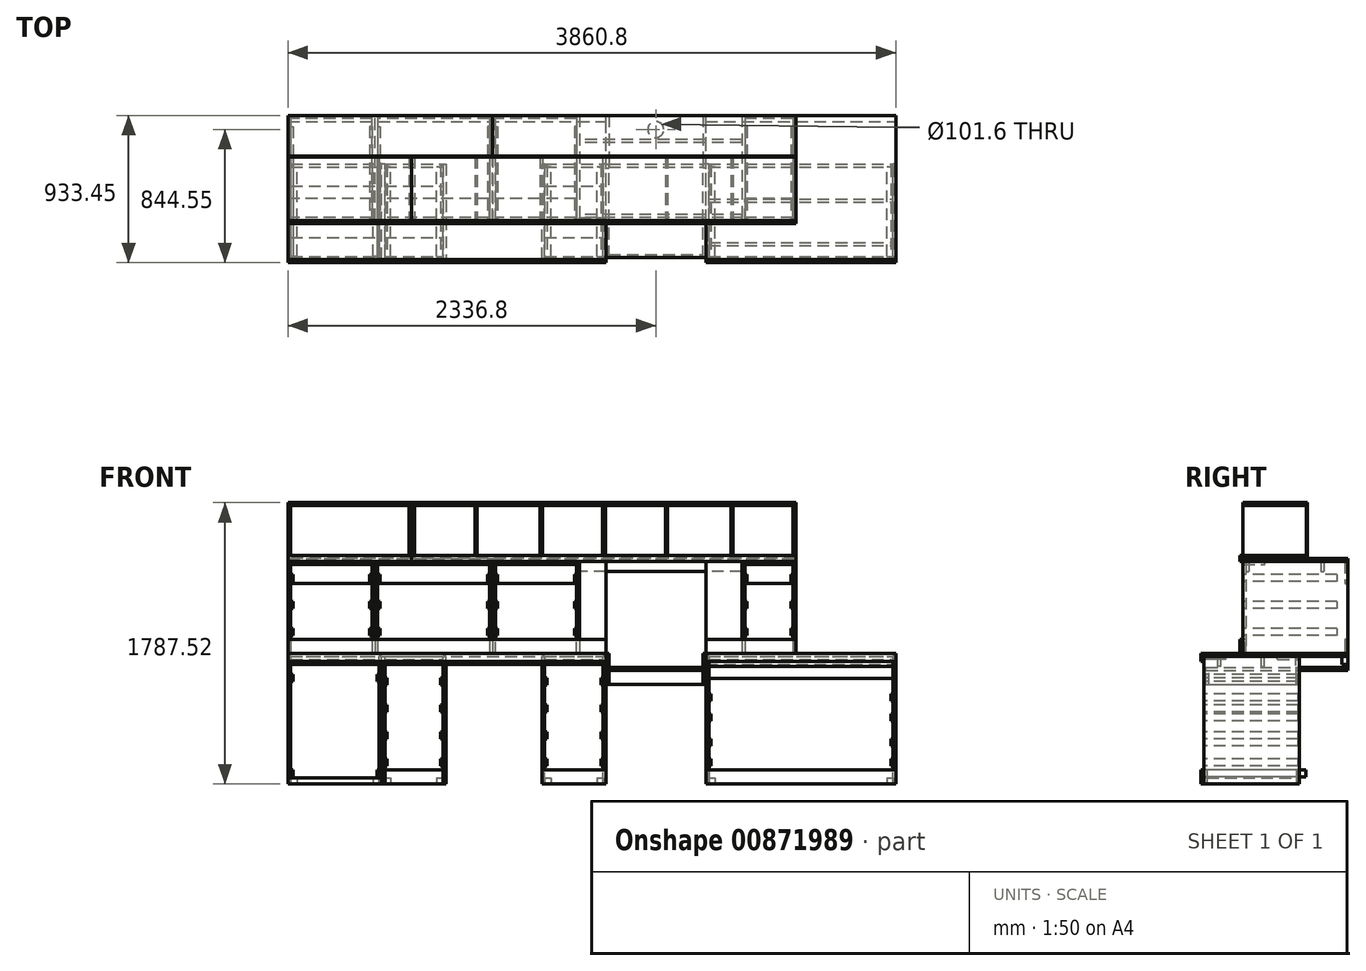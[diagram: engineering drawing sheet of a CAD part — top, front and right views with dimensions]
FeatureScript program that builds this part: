
annotation { "Feature Type Name" : "Feature", "Feature Type Description" : "" }
export const myFeature = defineFeature(function(context is Context, id is Id, definition is map)
    precondition{}
    {
        {
            var Q0;
            Q0=qCreatedBy(makeId("Top.planeOp"),FACE);
            var sketch = newSketch(context, id + "F0", { "sketchPlane" : qUnion([Q0])});
            skLineSegment(sketch, "E0.bottom", {"start": v(0, 0) * mm, "end": v(-19.05, 0) * mm});
            skLineSegment(sketch, "E0.top", {"start": v(0, 606.43) * mm, "end": v(-19.05, 606.43) * mm});
            skLineSegment(sketch, "E0.left", {"start": v(0, 0) * mm, "end": v(0, 606.43) * mm});
            skLineSegment(sketch, "E0.right", {"start": v(-19.05, 0) * mm, "end": v(-19.05, 606.43) * mm});
            skLineSegment(sketch, "E1.bottom", {"start": v(-1187.45, 0) * mm, "end": v(-1206.5, 0) * mm});
            skLineSegment(sketch, "E1.top", {"start": v(-1187.45, 606.42) * mm, "end": v(-1206.5, 606.42) * mm});
            skLineSegment(sketch, "E1.left", {"start": v(-1187.45, 0) * mm, "end": v(-1187.45, 606.42) * mm});
            skLineSegment(sketch, "E1.right", {"start": v(-1206.5, 0) * mm, "end": v(-1206.5, 606.42) * mm});
            skLineSegment(sketch, "E2.bottom", {"start": v(-1841.5, 0) * mm, "end": v(-1860.55, 0) * mm});
            skLineSegment(sketch, "E2.top", {"start": v(-1841.5, 606.42) * mm, "end": v(-1860.55, 606.42) * mm});
            skLineSegment(sketch, "E2.left", {"start": v(-1841.5, 0) * mm, "end": v(-1841.5, 606.42) * mm});
            skLineSegment(sketch, "E2.right", {"start": v(-1860.55, 0) * mm, "end": v(-1860.55, 606.42) * mm});
            skLineSegment(sketch, "E3.bottom", {"start": v(-2228.85, 0) * mm, "end": v(-2247.9, 0) * mm});
            skLineSegment(sketch, "E3.top", {"start": v(-2228.85, 606.42) * mm, "end": v(-2247.9, 606.42) * mm});
            skLineSegment(sketch, "E3.left", {"start": v(-2228.85, 0) * mm, "end": v(-2228.85, 606.42) * mm});
            skLineSegment(sketch, "E3.right", {"start": v(-2247.9, 0) * mm, "end": v(-2247.9, 606.42) * mm});
            skLineSegment(sketch, "E4.bottom", {"start": v(-2857.5, 0) * mm, "end": v(-2876.55, 0) * mm});
            skLineSegment(sketch, "E4.top", {"start": v(-2857.5, 606.42) * mm, "end": v(-2876.55, 606.42) * mm});
            skLineSegment(sketch, "E4.left", {"start": v(-2857.5, 0) * mm, "end": v(-2857.5, 606.42) * mm});
            skLineSegment(sketch, "E4.right", {"start": v(-2876.55, 0) * mm, "end": v(-2876.55, 606.42) * mm});
            skLineSegment(sketch, "E5.bottom", {"start": v(-3244.85, 0) * mm, "end": v(-3263.9, 0) * mm});
            skLineSegment(sketch, "E5.top", {"start": v(-3244.85, 606.42) * mm, "end": v(-3263.9, 606.42) * mm});
            skLineSegment(sketch, "E5.left", {"start": v(-3244.85, 0) * mm, "end": v(-3244.85, 606.42) * mm});
            skLineSegment(sketch, "E6", {"start": v(-3263.9, 606.42) * mm, "end": v(-3263.9, 0) * mm});
            skLineSegment(sketch, "E7.bottom", {"start": v(-3263.9, 0) * mm, "end": v(-3282.95, 0) * mm});
            skLineSegment(sketch, "E7.top", {"start": v(-3263.9, 606.42) * mm, "end": v(-3282.95, 606.42) * mm});
            skLineSegment(sketch, "E7.left", {"start": v(-3263.9, 0) * mm, "end": v(-3263.9, 606.42) * mm});
            skLineSegment(sketch, "E8", {"start": v(-3282.95, 606.42) * mm, "end": v(-3282.95, 0) * mm});
            skLineSegment(sketch, "E9.bottom", {"start": v(-3841.75, 0) * mm, "end": v(-3860.8, 0) * mm});
            skLineSegment(sketch, "E9.top", {"start": v(-3841.75, 606.42) * mm, "end": v(-3860.8, 606.42) * mm});
            skLineSegment(sketch, "E9.left", {"start": v(-3841.75, 0) * mm, "end": v(-3841.75, 606.42) * mm});
            skLineSegment(sketch, "E10", {"start": v(-3860.8, 606.42) * mm, "end": v(-3860.8, 0) * mm});
            skSolve(sketch);
        }
        {
            var Q0;
            Q0=makeQuery(id+"F0.imprint","IMPRINT",FACE,{"disambiguationData":[TD([[makeQuery(id+"F0.imprint","IMPRINT",EDGE,{"derivedFrom":sQuery(id+"F0.wireOp",EDGE,"E9.bottom")}),-1.0]])]});
            var Q1;
            Q1=makeQuery(id+"F0.imprint","IMPRINT",FACE,{"disambiguationData":[TD([[makeQuery(id+"F0.imprint","IMPRINT",EDGE,{"derivedFrom":sQuery(id+"F0.wireOp",EDGE,"E7.bottom")}),-1.0]])]});
            var Q2;
            Q2=makeQuery(id+"F0.imprint","IMPRINT",FACE,{"disambiguationData":[TD([[makeQuery(id+"F0.imprint","IMPRINT",EDGE,{"derivedFrom":sQuery(id+"F0.wireOp",EDGE,"E1.bottom")}),-1.0]])]});
            var Q3;
            Q3=makeQuery(id+"F0.imprint","IMPRINT",FACE,{"disambiguationData":[TD([[makeQuery(id+"F0.imprint","IMPRINT",EDGE,{"derivedFrom":sQuery(id+"F0.wireOp",EDGE,"E2.bottom")}),-1.0]])]});
            var Q4;
            Q4=makeQuery(id+"F0.imprint","IMPRINT",FACE,{"disambiguationData":[TD([[makeQuery(id+"F0.imprint","IMPRINT",EDGE,{"derivedFrom":sQuery(id+"F0.wireOp",EDGE,"E3.bottom")}),-1.0]])]});
            var Q5;
            Q5=makeQuery(id+"F0.imprint","IMPRINT",FACE,{"disambiguationData":[TD([[makeQuery(id+"F0.imprint","IMPRINT",EDGE,{"derivedFrom":sQuery(id+"F0.wireOp",EDGE,"E0.bottom")}),-1.0]])]});
            extrude(context, id + "F1", {"entities" : qUnion([Q0, Q1, Q2, Q3, Q4, Q5]), "oppositeDirection" : true, "depth" : 809.62 * mm, "offsetDistance" : 25.4 * mm});
        }
        {
            var Q0;
            Q0=qCreatedBy(makeId("Top.planeOp"),FACE);
            var sketch = newSketch(context, id + "F2", { "sketchPlane" : qUnion([Q0])});
            skPoint(sketch, "E11.0", {"position": v(-2857.5, 0) * mm});
            skPoint(sketch, "E11.1", {"position": v(-2876.55, 606.42) * mm});
            skLineSegment(sketch, "E12.bottom", {"start": v(-2857.5, 0) * mm, "end": v(-2876.55, 0) * mm});
            skLineSegment(sketch, "E12.top", {"start": v(-2857.5, 606.42) * mm, "end": v(-2876.55, 606.42) * mm});
            skLineSegment(sketch, "E12.left", {"start": v(-2857.5, 0) * mm, "end": v(-2857.5, 606.42) * mm});
            skLineSegment(sketch, "E12.right", {"start": v(-2876.55, 0) * mm, "end": v(-2876.55, 606.42) * mm});
            skPoint(sketch, "E13.0", {"position": v(-3263.9, 606.42) * mm});
            skPoint(sketch, "E13.1", {"position": v(-3244.85, 0) * mm});
            skLineSegment(sketch, "E14.bottom", {"start": v(-3263.9, 606.42) * mm, "end": v(-3244.85, 606.42) * mm});
            skLineSegment(sketch, "E14.top", {"start": v(-3263.9, 0) * mm, "end": v(-3244.85, 0) * mm});
            skLineSegment(sketch, "E14.left", {"start": v(-3263.9, 606.42) * mm, "end": v(-3263.9, 0) * mm});
            skLineSegment(sketch, "E14.right", {"start": v(-3244.85, 606.42) * mm, "end": v(-3244.85, 0) * mm});
            skSolve(sketch);
        }
        {
            var Q0;
            Q0 = qSketchRegion(id + "F2", true);
            var Q1;
            Q1=makeQuery(id+"F1.opExtrude","CAP_FACE",FACE,{"disambiguationData":[OSD([sQuery(id+"F0.wireOp",EDGE,"E7.bottom"),sQuery(id+"F0.wireOp",EDGE,"E7.top"),sQuery(id+"F0.wireOp",EDGE,"E7.left"),sQuery(id+"F0.wireOp",EDGE,"E8")])],"isStart":false});
            extrude(context, id + "F3", {"entities" : qUnion([Q0]), "endBound" : BoundingType.UP_TO_SURFACE, "oppositeDirection" : true, "depth" : 25.4 * mm, "endBoundEntityFace" : qUnion([Q1]), "offsetDistance" : 25.4 * mm});
        }
        {
            var Q0;
            Q0=makeQuery(id+"F1.opExtrude","SWEPT_FACE",FACE,{"disambiguationData":[OSD([sQuery(id+"F0.wireOp",EDGE,"E0.right")])]});
            var sketch = newSketch(context, id + "F4", { "sketchPlane" : qUnion([Q0])});
            skLineSegment(sketch, "E15.0", {"start": v(-606.43, -809.62) * mm, "end": v(-606.43, 0) * mm, "construction": true});
            skLineSegment(sketch, "E15.1", {"start": v(0, 0) * mm, "end": v(-606.43, 0) * mm, "construction": true});
            skLineSegment(sketch, "E15.2", {"start": v(0, -809.62) * mm, "end": v(0, 0) * mm, "construction": true});
            skLineSegment(sketch, "E16.bottom", {"start": v(-606.43, 0) * mm, "end": v(-587.38, 0) * mm});
            skLineSegment(sketch, "E16.top", {"start": v(-606.43, -139.7) * mm, "end": v(-587.38, -139.7) * mm});
            skLineSegment(sketch, "E16.left", {"start": v(-606.43, 0) * mm, "end": v(-606.43, -139.7) * mm});
            skLineSegment(sketch, "E16.right", {"start": v(-587.38, 0) * mm, "end": v(-587.38, -139.7) * mm});
            skLineSegment(sketch, "E17.bottom", {"start": v(-606.43, -809.62) * mm, "end": v(-587.38, -809.62) * mm});
            skLineSegment(sketch, "E17.top", {"start": v(-606.43, -720.73) * mm, "end": v(-587.38, -720.73) * mm});
            skLineSegment(sketch, "E17.left", {"start": v(-606.43, -809.62) * mm, "end": v(-606.43, -720.73) * mm});
            skLineSegment(sketch, "E17.right", {"start": v(-587.38, -809.62) * mm, "end": v(-587.38, -720.73) * mm});
            skLineSegment(sketch, "E18.bottom", {"start": v(0, 0) * mm, "end": v(-88.9, 0) * mm});
            skLineSegment(sketch, "E18.top", {"start": v(0, -19.05) * mm, "end": v(-88.9, -19.05) * mm});
            skLineSegment(sketch, "E18.left", {"start": v(0, 0) * mm, "end": v(0, -19.05) * mm});
            skLineSegment(sketch, "E18.right", {"start": v(-88.9, 0) * mm, "end": v(-88.9, -19.05) * mm});
            skLineSegment(sketch, "E19.bottom", {"start": v(0, -809.62) * mm, "end": v(-19.05, -809.62) * mm});
            skLineSegment(sketch, "E19.top", {"start": v(0, -720.73) * mm, "end": v(-19.05, -720.73) * mm});
            skLineSegment(sketch, "E19.left", {"start": v(0, -809.62) * mm, "end": v(0, -720.73) * mm});
            skLineSegment(sketch, "E19.right", {"start": v(-19.05, -809.62) * mm, "end": v(-19.05, -720.73) * mm});
            skSolve(sketch);
        }
        {
            var Q0;
            Q0 = qSketchRegion(id + "F4", true);
            var Q1;
            Q1=makeQuery(id+"F1.opExtrude","SWEPT_FACE",FACE,{"disambiguationData":[OSD([sQuery(id+"F0.wireOp",EDGE,"E1.left")])]});
            extrude(context, id + "F5", {"entities" : qUnion([Q0]), "endBound" : BoundingType.UP_TO_SURFACE, "depth" : 25.4 * mm, "endBoundEntityFace" : qUnion([Q1]), "offsetDistance" : 25.4 * mm});
        }
        {
            var Q0;
            Q0=makeQuery(id+"F1.opExtrude","SWEPT_FACE",FACE,{"disambiguationData":[OSD([sQuery(id+"F0.wireOp",EDGE,"E2.right")])]});
            var sketch = newSketch(context, id + "F6", { "sketchPlane" : qUnion([Q0])});
            skLineSegment(sketch, "E20.1", {"start": v(0, 0) * mm, "end": v(-606.42, 0) * mm, "construction": true});
            skLineSegment(sketch, "E21.bottom", {"start": v(-606.42, 0) * mm, "end": v(-466.72, 0) * mm});
            skLineSegment(sketch, "E21.top", {"start": v(-606.42, -19.05) * mm, "end": v(-466.72, -19.05) * mm});
            skLineSegment(sketch, "E21.left", {"start": v(-606.42, 0) * mm, "end": v(-606.42, -19.05) * mm});
            skLineSegment(sketch, "E21.right", {"start": v(-466.72, 0) * mm, "end": v(-466.72, -19.05) * mm});
            skLineSegment(sketch, "E22.bottom", {"start": v(-606.42, -809.62) * mm, "end": v(-587.37, -809.62) * mm});
            skLineSegment(sketch, "E22.top", {"start": v(-606.42, -720.73) * mm, "end": v(-587.37, -720.73) * mm});
            skLineSegment(sketch, "E22.left", {"start": v(-606.42, -809.62) * mm, "end": v(-606.42, -720.73) * mm});
            skLineSegment(sketch, "E22.right", {"start": v(-587.37, -809.62) * mm, "end": v(-587.37, -720.73) * mm});
            skLineSegment(sketch, "E23.bottom", {"start": v(0, 0) * mm, "end": v(-139.7, 0) * mm});
            skLineSegment(sketch, "E23.top", {"start": v(0, -19.05) * mm, "end": v(-139.7, -19.05) * mm});
            skLineSegment(sketch, "E23.left", {"start": v(0, 0) * mm, "end": v(0, -19.05) * mm});
            skLineSegment(sketch, "E23.right", {"start": v(-139.7, 0) * mm, "end": v(-139.7, -19.05) * mm});
            skLineSegment(sketch, "E24.bottom", {"start": v(0, -809.62) * mm, "end": v(-19.05, -809.62) * mm});
            skLineSegment(sketch, "E24.top", {"start": v(0, -720.73) * mm, "end": v(-19.05, -720.73) * mm});
            skLineSegment(sketch, "E24.left", {"start": v(0, -809.62) * mm, "end": v(0, -720.73) * mm});
            skLineSegment(sketch, "E24.right", {"start": v(-19.05, -809.62) * mm, "end": v(-19.05, -720.73) * mm});
            skSolve(sketch);
        }
        {
            var Q0;
            Q0 = qSketchRegion(id + "F6", true);
            var Q1;
            Q1=makeQuery(id+"F1.opExtrude","SWEPT_FACE",FACE,{"disambiguationData":[OSD([sQuery(id+"F0.wireOp",EDGE,"E3.left")])]});
            extrude(context, id + "F7", {"entities" : qUnion([Q0]), "endBound" : BoundingType.UP_TO_SURFACE, "depth" : 25.4 * mm, "endBoundEntityFace" : qUnion([Q1]), "offsetDistance" : 25.4 * mm});
        }
        {
            var Q0;
            Q0=makeQuery(id+"F1.opExtrude","SWEPT_FACE",FACE,{"disambiguationData":[OSD([sQuery(id+"F0.wireOp",EDGE,"E8")])]});
            var sketch = newSketch(context, id + "F8", { "sketchPlane" : qUnion([Q0])});
            skLineSegment(sketch, "E25.1", {"start": v(-606.42, 0) * mm, "end": v(0, 0) * mm, "construction": true});
            skLineSegment(sketch, "E26.bottom", {"start": v(-606.42, 0) * mm, "end": v(-466.72, 0) * mm});
            skLineSegment(sketch, "E26.top", {"start": v(-606.42, -19.05) * mm, "end": v(-466.72, -19.05) * mm});
            skLineSegment(sketch, "E26.left", {"start": v(-606.42, 0) * mm, "end": v(-606.42, -19.05) * mm});
            skLineSegment(sketch, "E26.right", {"start": v(-466.72, 0) * mm, "end": v(-466.72, -19.05) * mm});
            skLineSegment(sketch, "E27.bottom", {"start": v(-606.42, -809.62) * mm, "end": v(-587.37, -809.62) * mm});
            skLineSegment(sketch, "E27.top", {"start": v(-606.42, -771.53) * mm, "end": v(-587.37, -771.53) * mm});
            skLineSegment(sketch, "E27.left", {"start": v(-606.42, -809.62) * mm, "end": v(-606.42, -771.53) * mm});
            skLineSegment(sketch, "E27.right", {"start": v(-587.37, -809.62) * mm, "end": v(-587.37, -771.53) * mm});
            skLineSegment(sketch, "E28.bottom", {"start": v(0, 0) * mm, "end": v(-139.7, 0) * mm});
            skLineSegment(sketch, "E28.top", {"start": v(0, -19.05) * mm, "end": v(-139.7, -19.05) * mm});
            skLineSegment(sketch, "E28.left", {"start": v(0, 0) * mm, "end": v(0, -19.05) * mm});
            skLineSegment(sketch, "E28.right", {"start": v(-139.7, 0) * mm, "end": v(-139.7, -19.05) * mm});
            skLineSegment(sketch, "E29.bottom", {"start": v(0, -809.62) * mm, "end": v(-19.05, -809.62) * mm});
            skLineSegment(sketch, "E29.top", {"start": v(0, -771.53) * mm, "end": v(-19.05, -771.53) * mm});
            skLineSegment(sketch, "E29.left", {"start": v(0, -809.62) * mm, "end": v(0, -771.53) * mm});
            skLineSegment(sketch, "E29.right", {"start": v(-19.05, -809.62) * mm, "end": v(-19.05, -771.53) * mm});
            skSolve(sketch);
        }
        {
            var Q0;
            Q0 = qSketchRegion(id + "F8", true);
            var Q1;
            Q1=makeQuery(id+"F1.opExtrude","SWEPT_FACE",FACE,{"disambiguationData":[OSD([sQuery(id+"F0.wireOp",EDGE,"E9.left")])]});
            extrude(context, id + "F9", {"entities" : qUnion([Q0]), "endBound" : BoundingType.UP_TO_SURFACE, "depth" : 25.4 * mm, "endBoundEntityFace" : qUnion([Q1]), "offsetDistance" : 25.4 * mm});
        }
        {
            var Q0;
            Q0=makeQuery(id+"F1.opExtrude","SWEPT_FACE",FACE,{"disambiguationData":[OSD([sQuery(id+"F0.wireOp",EDGE,"E0.right")])]});
            var sketch = newSketch(context, id + "F10", { "sketchPlane" : qUnion([Q0])});
            skLineSegment(sketch, "E30.bottom", {"start": v(-384.18, 0) * mm, "end": v(-365.13, 0) * mm});
            skLineSegment(sketch, "E30.top", {"start": v(-384.18, -63.5) * mm, "end": v(-365.13, -63.5) * mm});
            skLineSegment(sketch, "E30.left", {"start": v(-384.18, 0) * mm, "end": v(-384.18, -63.5) * mm});
            skLineSegment(sketch, "E30.right", {"start": v(-365.13, 0) * mm, "end": v(-365.13, -63.5) * mm});
            skPoint(sketch, "E31.0", {"position": v(-88.9, 0) * mm});
            skLineSegment(sketch, "E32.bottom", {"start": v(-88.9, 0) * mm, "end": v(-107.95, 0) * mm});
            skLineSegment(sketch, "E32.top", {"start": v(-88.9, -63.5) * mm, "end": v(-107.95, -63.5) * mm});
            skLineSegment(sketch, "E32.left", {"start": v(-88.9, 0) * mm, "end": v(-88.9, -63.5) * mm});
            skLineSegment(sketch, "E32.right", {"start": v(-107.95, 0) * mm, "end": v(-107.95, -63.5) * mm});
            skSolve(sketch);
        }
        {
            var Q0;
            Q0 = qSketchRegion(id + "F10", true);
            var Q1;
            Q1=makeQuery(id+"F1.opExtrude","SWEPT_FACE",FACE,{"disambiguationData":[OSD([sQuery(id+"F0.wireOp",EDGE,"E1.left")])]});
            extrude(context, id + "F11", {"entities" : qUnion([Q0]), "endBound" : BoundingType.UP_TO_SURFACE, "depth" : 25.4 * mm, "endBoundEntityFace" : qUnion([Q1]), "offsetDistance" : 25.4 * mm});
        }
        {
            var Q0;
            Q0=qCreatedBy(makeId("Top.planeOp"),FACE);
            var sketch = newSketch(context, id + "F12", { "sketchPlane" : qUnion([Q0])});
            skPoint(sketch, "E33.0", {"position": v(-1206.5, 606.42) * mm});
            skLineSegment(sketch, "E34.bottom", {"start": v(0, 0) * mm, "end": v(-1206.5, 0) * mm});
            skLineSegment(sketch, "E34.top", {"start": v(0, 914.4) * mm, "end": v(-1206.5, 914.4) * mm});
            skLineSegment(sketch, "E34.left", {"start": v(0, 0) * mm, "end": v(0, 914.4) * mm});
            skLineSegment(sketch, "E34.right", {"start": v(-1206.5, 0) * mm, "end": v(-1206.5, 914.4) * mm});
            skPoint(sketch, "E35.0", {"position": v(-1841.5, 0) * mm});
            skPoint(sketch, "E35.1", {"position": v(-3860.8, 606.42) * mm});
            skLineSegment(sketch, "E36.bottom", {"start": v(-1841.5, 0) * mm, "end": v(-3860.8, 0) * mm});
            skLineSegment(sketch, "E36.top", {"start": v(-1841.5, 914.4) * mm, "end": v(-3860.8, 914.4) * mm});
            skLineSegment(sketch, "E36.left", {"start": v(-1841.5, 0) * mm, "end": v(-1841.5, 914.4) * mm});
            skLineSegment(sketch, "E36.right", {"start": v(-3860.8, 0) * mm, "end": v(-3860.8, 914.4) * mm});
            skLineSegment(sketch, "E37.0", {"start": v(-3860.8, 606.42) * mm, "end": v(-3860.8, 0) * mm, "construction": true});
            skLineSegment(sketch, "E38.0", {"start": v(-1206.5, 0) * mm, "end": v(-1206.5, 606.42) * mm, "construction": true});
            skSolve(sketch);
        }
        {
            var Q0;
            Q0 = qSketchRegion(id + "F12", true);
            extrude(context, id + "F13", {"entities" : qUnion([Q0]), "depth" : 19.05 * mm, "offsetDistance" : 25.4 * mm});
        }
        {
            var Q0;
            Q0=makeQuery(id+"F13.opExtrude","SWEPT_FACE",FACE,{"disambiguationData":[OSD([sQuery(id+"F12.wireOp",EDGE,"E34.left")])]});
            var sketch = newSketch(context, id + "F14", { "sketchPlane" : qUnion([Q0])});
            skLineSegment(sketch, "E39.bottom", {"start": v(876.3, 0) * mm, "end": v(914.4, 0) * mm});
            skLineSegment(sketch, "E39.top", {"start": v(876.3, -50.8) * mm, "end": v(914.4, -50.8) * mm});
            skLineSegment(sketch, "E39.left", {"start": v(876.3, 0) * mm, "end": v(876.3, -50.8) * mm});
            skLineSegment(sketch, "E39.right", {"start": v(914.4, 0) * mm, "end": v(914.4, -50.8) * mm});
            skSolve(sketch);
        }
        {
            var Q0;
            Q0 = qSketchRegion(id + "F14", true);
            var Q1;
            Q1=makeQuery(id+"F13.opExtrude","SWEPT_FACE",FACE,{"disambiguationData":[OSD([sQuery(id+"F12.wireOp",EDGE,"E34.right")])]});
            extrude(context, id + "F15", {"entities" : qUnion([Q0]), "endBound" : BoundingType.UP_TO_SURFACE, "oppositeDirection" : true, "depth" : 25.4 * mm, "endBoundEntityFace" : qUnion([Q1]), "offsetDistance" : 25.4 * mm});
        }
        {
            var Q0;
            Q0=makeQuery(id+"F13.opExtrude","SWEPT_FACE",FACE,{"disambiguationData":[OSD([sQuery(id+"F12.wireOp",EDGE,"E36.left")])]});
            var sketch = newSketch(context, id + "F16", { "sketchPlane" : qUnion([Q0])});
            skLineSegment(sketch, "E40.bottom", {"start": v(876.3, 0) * mm, "end": v(914.4, 0) * mm});
            skLineSegment(sketch, "E40.top", {"start": v(876.3, -50.8) * mm, "end": v(914.4, -50.8) * mm});
            skLineSegment(sketch, "E40.left", {"start": v(876.3, 0) * mm, "end": v(876.3, -50.8) * mm});
            skLineSegment(sketch, "E40.right", {"start": v(914.4, 0) * mm, "end": v(914.4, -50.8) * mm});
            skSolve(sketch);
        }
        {
            var Q0;
            Q0=makeQuery(id+"F16.imprint","IMPRINT",FACE,{"disambiguationData":[TD([[makeQuery(id+"F16.imprint","IMPRINT",EDGE,{"derivedFrom":sQuery(id+"F16.wireOp",EDGE,"E40.bottom")}),-1.0]])]});
            var Q1;
            Q1=makeQuery(id+"F13.opExtrude","SWEPT_FACE",FACE,{"disambiguationData":[OSD([sQuery(id+"F12.wireOp",EDGE,"E36.right")])]});
            extrude(context, id + "F17", {"entities" : qUnion([Q0]), "endBound" : BoundingType.UP_TO_SURFACE, "oppositeDirection" : true, "depth" : 25.4 * mm, "endBoundEntityFace" : qUnion([Q1]), "offsetDistance" : 25.4 * mm});
        }
        {
            var Q0;
            Q0=makeQuery(id+"F13.opExtrude","CAP_FACE",FACE,{"disambiguationData":[OSD([sQuery(id+"F12.wireOp",EDGE,"E34.bottom"),sQuery(id+"F12.wireOp",EDGE,"E34.top"),sQuery(id+"F12.wireOp",EDGE,"E34.left"),sQuery(id+"F12.wireOp",EDGE,"E34.right")])],"isStart":false});
            cPlane(context, id + "F18", {"entities" : qUnion([Q0]), "cplaneType" : CPlaneType.OFFSET, "offset" : 88.9 * mm, "oppositeDirection" : true, "width" : 152.4 * mm, "height" : 152.4 * mm});
        }
        {
            var Q0;
            Q0=qCreatedBy(id+"F18.planeOp",FACE);
            var sketch = newSketch(context, id + "F19", { "sketchPlane" : qUnion([Q0])});
            skLineSegment(sketch, "E41.0", {"start": v(-1841.5, 0) * mm, "end": v(-3860.8, 0) * mm, "construction": true});
            skLineSegment(sketch, "E41.1", {"start": v(0, 0) * mm, "end": v(-1206.5, 0) * mm, "construction": true});
            skLineSegment(sketch, "E41.2", {"start": v(-1206.5, 0) * mm, "end": v(-1206.5, 914.4) * mm, "construction": true});
            skLineSegment(sketch, "E41.3", {"start": v(-1841.5, 0) * mm, "end": v(-1841.5, 914.4) * mm, "construction": true});
            skLineSegment(sketch, "E42.bottom", {"start": v(-1841.5, 12.7) * mm, "end": v(-1206.5, 12.7) * mm});
            skLineSegment(sketch, "E42.top", {"start": v(-1841.5, 914.4) * mm, "end": v(-1206.5, 914.4) * mm});
            skLineSegment(sketch, "E42.left", {"start": v(-1841.5, 12.7) * mm, "end": v(-1841.5, 914.4) * mm});
            skLineSegment(sketch, "E42.right", {"start": v(-1206.5, 12.7) * mm, "end": v(-1206.5, 914.4) * mm});
            skSolve(sketch);
        }
        {
            var Q0;
            Q0=makeQuery(id+"F19.imprint","IMPRINT",FACE,{"disambiguationData":[TD([[makeQuery(id+"F19.imprint","IMPRINT",EDGE,{"derivedFrom":sQuery(id+"F19.wireOp",EDGE,"E42.bottom")}),1.0]])]});
            extrude(context, id + "F20", {"entities" : qUnion([Q0]), "oppositeDirection" : true, "depth" : 19.05 * mm, "offsetDistance" : 25.4 * mm});
        }
        {
            var Q0;
            Q0=makeQuery(id+"F20.opExtrude","CAP_FACE",FACE,{"disambiguationData":[OSD([sQuery(id+"F19.wireOp",EDGE,"E42.bottom"),sQuery(id+"F19.wireOp",EDGE,"E42.top"),sQuery(id+"F19.wireOp",EDGE,"E42.left"),sQuery(id+"F19.wireOp",EDGE,"E42.right")])],"isStart":false});
            var sketch = newSketch(context, id + "F21", { "sketchPlane" : qUnion([Q0])});
            skPoint(sketch, "E43.0", {"position": v(-1841.5, -606.42) * mm});
            skPoint(sketch, "E44.0", {"position": v(-1206.5, -606.42) * mm});
            skLineSegment(sketch, "E45.bottom", {"start": v(-1841.5, -12.7) * mm, "end": v(-1822.45, -12.7) * mm});
            skLineSegment(sketch, "E45.top", {"start": v(-1841.5, -606.42) * mm, "end": v(-1822.45, -606.42) * mm});
            skLineSegment(sketch, "E45.left", {"start": v(-1841.5, -12.7) * mm, "end": v(-1841.5, -606.42) * mm});
            skLineSegment(sketch, "E45.right", {"start": v(-1822.45, -12.7) * mm, "end": v(-1822.45, -606.42) * mm});
            skLineSegment(sketch, "E46.bottom", {"start": v(-1206.5, -12.7) * mm, "end": v(-1225.55, -12.7) * mm});
            skLineSegment(sketch, "E46.top", {"start": v(-1206.5, -606.42) * mm, "end": v(-1225.55, -606.42) * mm});
            skLineSegment(sketch, "E46.left", {"start": v(-1206.5, -12.7) * mm, "end": v(-1206.5, -606.42) * mm});
            skLineSegment(sketch, "E46.right", {"start": v(-1225.55, -12.7) * mm, "end": v(-1225.55, -606.42) * mm});
            skSolve(sketch);
        }
        {
            var Q0;
            Q0 = qSketchRegion(id + "F21", true);
            extrude(context, id + "F22", {"entities" : qUnion([Q0]), "depth" : 88.9 * mm, "offsetDistance" : 25.4 * mm});
        }
        {
            var Q0;
            Q0=makeQuery(id+"F20.opExtrude","CAP_FACE",FACE,{"disambiguationData":[OSD([sQuery(id+"F19.wireOp",EDGE,"E42.bottom"),sQuery(id+"F19.wireOp",EDGE,"E42.top"),sQuery(id+"F19.wireOp",EDGE,"E42.left"),sQuery(id+"F19.wireOp",EDGE,"E42.right")])],"isStart":false});
            var sketch = newSketch(context, id + "F23", { "sketchPlane" : qUnion([Q0])});
            skPoint(sketch, "E47.0", {"position": v(-1822.45, -12.7) * mm});
            skPoint(sketch, "E47.1", {"position": v(-1225.55, -12.7) * mm});
            skPoint(sketch, "E47.2", {"position": v(-1225.55, -606.42) * mm});
            skPoint(sketch, "E47.3", {"position": v(-1822.45, -606.42) * mm});
            skLineSegment(sketch, "E48.bottom", {"start": v(-1822.45, -12.7) * mm, "end": v(-1225.55, -12.7) * mm});
            skLineSegment(sketch, "E48.top", {"start": v(-1822.45, -31.75) * mm, "end": v(-1225.55, -31.75) * mm});
            skLineSegment(sketch, "E48.left", {"start": v(-1822.45, -12.7) * mm, "end": v(-1822.45, -31.75) * mm});
            skLineSegment(sketch, "E48.right", {"start": v(-1225.55, -12.7) * mm, "end": v(-1225.55, -31.75) * mm});
            skLineSegment(sketch, "E49.bottom", {"start": v(-1822.45, -606.42) * mm, "end": v(-1225.55, -606.42) * mm});
            skLineSegment(sketch, "E49.top", {"start": v(-1822.45, -587.37) * mm, "end": v(-1225.55, -587.37) * mm});
            skLineSegment(sketch, "E49.left", {"start": v(-1822.45, -606.42) * mm, "end": v(-1822.45, -587.37) * mm});
            skLineSegment(sketch, "E49.right", {"start": v(-1225.55, -606.42) * mm, "end": v(-1225.55, -587.37) * mm});
            skSolve(sketch);
        }
        {
            var Q0;
            Q0 = qSketchRegion(id + "F23", true);
            var Q1;
            Q1=makeQuery(id+"F22.opExtrude","CAP_FACE",FACE,{"disambiguationData":[OSD([sQuery(id+"F21.wireOp",EDGE,"E45.bottom"),sQuery(id+"F21.wireOp",EDGE,"E45.top"),sQuery(id+"F21.wireOp",EDGE,"E45.left"),sQuery(id+"F21.wireOp",EDGE,"E45.right")])],"isStart":false});
            extrude(context, id + "F24", {"entities" : qUnion([Q0]), "endBound" : BoundingType.UP_TO_SURFACE, "depth" : 25.4 * mm, "endBoundEntityFace" : qUnion([Q1]), "offsetDistance" : 25.4 * mm});
        }
        {
            var Q0;
            Q0=makeQuery(id+"F20.opExtrude","CAP_FACE",FACE,{"disambiguationData":[OSD([sQuery(id+"F19.wireOp",EDGE,"E42.bottom"),sQuery(id+"F19.wireOp",EDGE,"E42.top"),sQuery(id+"F19.wireOp",EDGE,"E42.left"),sQuery(id+"F19.wireOp",EDGE,"E42.right")])],"isStart":true});
            var sketch = newSketch(context, id + "F25", { "sketchPlane" : qUnion([Q0])});
            skLineSegment(sketch, "E50.0", {"start": v(-1841.5, 914.4) * mm, "end": v(-1206.5, 914.4) * mm, "construction": true});
            skLineSegment(sketch, "E51", {"start": v(-1524, 914.4) * mm, "end": v(-1524, 825.5) * mm, "construction": true});
            skCircle(sketch, "E52", {"center": v(-1524, 825.5) * mm, "radius": 50.8 * mm});
            skSolve(sketch);
        }
        {
            var Q0;
            Q0 = qSketchRegion(id + "F25", true);
            extrude(context, id + "F26", {"entities" : qUnion([Q0]), "operationType" : NewBodyOperationType.REMOVE, "endBound" : BoundingType.UP_TO_NEXT, "oppositeDirection" : true, "depth" : 25.4 * mm, "offsetDistance" : 25.4 * mm});
        }
        {
            var Q0;
            Q0=makeQuery(id+"F20.opExtrude","CAP_FACE",FACE,{"disambiguationData":[OSD([sQuery(id+"F19.wireOp",EDGE,"E42.bottom"),sQuery(id+"F19.wireOp",EDGE,"E42.top"),sQuery(id+"F19.wireOp",EDGE,"E42.left"),sQuery(id+"F19.wireOp",EDGE,"E42.right")])],"isStart":true});
            var sketch = newSketch(context, id + "F27", { "sketchPlane" : qUnion([Q0])});
            skLineSegment(sketch, "E53.2", {"start": v(-1841.5, 0) * mm, "end": v(-1841.5, 914.4) * mm, "construction": true});
            skLineSegment(sketch, "E53.3", {"start": v(-1206.5, 0) * mm, "end": v(-1206.5, 914.4) * mm, "construction": true});
            skPoint(sketch, "E54.0", {"position": v(-1841.5, 606.42) * mm});
            skPoint(sketch, "E54.1", {"position": v(-1206.5, 606.42) * mm});
            skLineSegment(sketch, "E55.bottom", {"start": v(-1841.5, 914.4) * mm, "end": v(-1822.45, 914.4) * mm});
            skLineSegment(sketch, "E55.top", {"start": v(-1841.5, 581.02) * mm, "end": v(-1822.45, 581.02) * mm});
            skLineSegment(sketch, "E55.left", {"start": v(-1841.5, 914.4) * mm, "end": v(-1841.5, 581.02) * mm});
            skLineSegment(sketch, "E55.right", {"start": v(-1822.45, 914.4) * mm, "end": v(-1822.45, 581.02) * mm});
            skLineSegment(sketch, "E56.bottom", {"start": v(-1206.5, 914.4) * mm, "end": v(-1225.55, 914.4) * mm});
            skLineSegment(sketch, "E56.top", {"start": v(-1206.5, 581.02) * mm, "end": v(-1225.55, 581.02) * mm});
            skLineSegment(sketch, "E56.left", {"start": v(-1206.5, 914.4) * mm, "end": v(-1206.5, 581.02) * mm});
            skLineSegment(sketch, "E56.right", {"start": v(-1225.55, 914.4) * mm, "end": v(-1225.55, 581.02) * mm});
            skSolve(sketch);
        }
        {
            var Q0;
            Q0 = qSketchRegion(id + "F27", true);
            var Q1;
            Q1=makeQuery(id+"F13.opExtrude","CAP_FACE",FACE,{"disambiguationData":[OSD([sQuery(id+"F12.wireOp",EDGE,"E36.bottom"),sQuery(id+"F12.wireOp",EDGE,"E36.top"),sQuery(id+"F12.wireOp",EDGE,"E36.left"),sQuery(id+"F12.wireOp",EDGE,"E36.right")])],"isStart":false});
            extrude(context, id + "F28", {"entities" : qUnion([Q0]), "endBound" : BoundingType.UP_TO_SURFACE, "depth" : 25.4 * mm, "endBoundEntityFace" : qUnion([Q1]), "offsetDistance" : 25.4 * mm});
        }
        {
            var Q0;
            Q0=makeQuery(id+"F3.opExtrude","SWEPT_FACE",FACE,{"disambiguationData":[OSD([sQuery(id+"F2.wireOp",EDGE,"E12.right")])]});
            var sketch = newSketch(context, id + "F29", { "sketchPlane" : qUnion([Q0])});
            skLineSegment(sketch, "E57.1", {"start": v(-606.42, 0) * mm, "end": v(0, 0) * mm, "construction": true});
            skLineSegment(sketch, "E58.bottom", {"start": v(-606.42, 0) * mm, "end": v(-466.72, 0) * mm});
            skLineSegment(sketch, "E58.top", {"start": v(-606.42, -19.05) * mm, "end": v(-466.72, -19.05) * mm});
            skLineSegment(sketch, "E58.left", {"start": v(-606.42, 0) * mm, "end": v(-606.42, -19.05) * mm});
            skLineSegment(sketch, "E58.right", {"start": v(-466.72, 0) * mm, "end": v(-466.72, -19.05) * mm});
            skLineSegment(sketch, "E59.bottom", {"start": v(-606.42, -809.62) * mm, "end": v(-587.37, -809.62) * mm});
            skLineSegment(sketch, "E59.top", {"start": v(-606.42, -720.73) * mm, "end": v(-587.37, -720.73) * mm});
            skLineSegment(sketch, "E59.left", {"start": v(-606.42, -809.62) * mm, "end": v(-606.42, -720.73) * mm});
            skLineSegment(sketch, "E59.right", {"start": v(-587.37, -809.62) * mm, "end": v(-587.37, -720.73) * mm});
            skLineSegment(sketch, "E60.bottom", {"start": v(0, 0) * mm, "end": v(-139.7, 0) * mm});
            skLineSegment(sketch, "E60.top", {"start": v(0, -19.05) * mm, "end": v(-139.7, -19.05) * mm});
            skLineSegment(sketch, "E60.left", {"start": v(0, 0) * mm, "end": v(0, -19.05) * mm});
            skLineSegment(sketch, "E60.right", {"start": v(-139.7, 0) * mm, "end": v(-139.7, -19.05) * mm});
            skLineSegment(sketch, "E61.bottom", {"start": v(0, -809.62) * mm, "end": v(-19.05, -809.62) * mm});
            skLineSegment(sketch, "E61.top", {"start": v(0, -720.73) * mm, "end": v(-19.05, -720.73) * mm});
            skLineSegment(sketch, "E61.left", {"start": v(0, -809.62) * mm, "end": v(0, -720.73) * mm});
            skLineSegment(sketch, "E61.right", {"start": v(-19.05, -809.62) * mm, "end": v(-19.05, -720.73) * mm});
            skSolve(sketch);
        }
        {
            var Q0;
            Q0 = qSketchRegion(id + "F29", true);
            var Q1;
            Q1=makeQuery(id+"F3.opExtrude","SWEPT_FACE",FACE,{"disambiguationData":[OSD([sQuery(id+"F2.wireOp",EDGE,"E14.right")])]});
            extrude(context, id + "F30", {"entities" : qUnion([Q0]), "endBound" : BoundingType.UP_TO_SURFACE, "depth" : 25.4 * mm, "endBoundEntityFace" : qUnion([Q1]), "offsetDistance" : 25.4 * mm});
        }
        {
            var Q0;
            Q0=makeQuery(id+"F13.opExtrude","CAP_FACE",FACE,{"disambiguationData":[OSD([sQuery(id+"F12.wireOp",EDGE,"E36.bottom"),sQuery(id+"F12.wireOp",EDGE,"E36.top"),sQuery(id+"F12.wireOp",EDGE,"E36.left"),sQuery(id+"F12.wireOp",EDGE,"E36.right")])],"isStart":false});
            var sketch = newSketch(context, id + "F31", { "sketchPlane" : qUnion([Q0])});
            skLineSegment(sketch, "E62.0", {"start": v(-1841.5, 0) * mm, "end": v(-1841.5, 914.4) * mm, "construction": true});
            skLineSegment(sketch, "E62.1", {"start": v(-1841.5, 914.4) * mm, "end": v(-3860.8, 914.4) * mm, "construction": true});
            skLineSegment(sketch, "E62.2", {"start": v(-3860.8, 0) * mm, "end": v(-3860.8, 914.4) * mm, "construction": true});
            skLineSegment(sketch, "E63.bottom", {"start": v(-2028.82, 914.4) * mm, "end": v(-2009.77, 914.4) * mm});
            skLineSegment(sketch, "E63.top", {"start": v(-2028.82, 247.65) * mm, "end": v(-2009.77, 247.65) * mm});
            skLineSegment(sketch, "E63.left", {"start": v(-2028.82, 914.4) * mm, "end": v(-2028.82, 247.65) * mm});
            skLineSegment(sketch, "E63.right", {"start": v(-2009.77, 914.4) * mm, "end": v(-2009.77, 247.65) * mm});
            skLineSegment(sketch, "E64.bottom", {"start": v(-3860.8, 914.4) * mm, "end": v(-3841.75, 914.4) * mm});
            skLineSegment(sketch, "E64.top", {"start": v(-3860.8, 247.65) * mm, "end": v(-3841.75, 247.65) * mm});
            skLineSegment(sketch, "E64.left", {"start": v(-3860.8, 914.4) * mm, "end": v(-3860.8, 247.65) * mm});
            skLineSegment(sketch, "E64.right", {"start": v(-3841.75, 914.4) * mm, "end": v(-3841.75, 247.65) * mm});
            skLineSegment(sketch, "E65", {"start": v(-2028.82, 247.65) * mm, "end": v(-2543.17, 247.65) * mm, "construction": true});
            skLineSegment(sketch, "E66", {"start": v(-3841.75, 247.65) * mm, "end": v(-3327.4, 247.65) * mm, "construction": true});
            skLineSegment(sketch, "E67.bottom", {"start": v(-2543.17, 247.65) * mm, "end": v(-2562.22, 247.65) * mm});
            skLineSegment(sketch, "E67.top", {"start": v(-2543.17, 914.4) * mm, "end": v(-2562.22, 914.4) * mm});
            skLineSegment(sketch, "E67.left", {"start": v(-2543.17, 247.65) * mm, "end": v(-2543.17, 914.4) * mm});
            skLineSegment(sketch, "E67.right", {"start": v(-2562.22, 247.65) * mm, "end": v(-2562.22, 914.4) * mm});
            skLineSegment(sketch, "E68.bottom", {"start": v(-3327.4, 247.65) * mm, "end": v(-3308.35, 247.65) * mm});
            skLineSegment(sketch, "E68.top", {"start": v(-3327.4, 914.4) * mm, "end": v(-3308.35, 914.4) * mm});
            skLineSegment(sketch, "E68.left", {"start": v(-3327.4, 247.65) * mm, "end": v(-3327.4, 914.4) * mm});
            skLineSegment(sketch, "E68.right", {"start": v(-3308.35, 247.65) * mm, "end": v(-3308.35, 914.4) * mm});
            skLineSegment(sketch, "E69.0", {"start": v(-1206.5, 0) * mm, "end": v(-1206.5, 914.4) * mm, "construction": true});
            skLineSegment(sketch, "E69.1", {"start": v(0, 914.4) * mm, "end": v(-1206.5, 914.4) * mm, "construction": true});
            skLineSegment(sketch, "E70.bottom", {"start": v(-977.9, 914.4) * mm, "end": v(-958.85, 914.4) * mm});
            skLineSegment(sketch, "E70.top", {"start": v(-977.9, 247.65) * mm, "end": v(-958.85, 247.65) * mm});
            skLineSegment(sketch, "E70.left", {"start": v(-977.9, 914.4) * mm, "end": v(-977.9, 247.65) * mm});
            skLineSegment(sketch, "E70.right", {"start": v(-958.85, 914.4) * mm, "end": v(-958.85, 247.65) * mm});
            skLineSegment(sketch, "E71.bottom", {"start": v(-635, 914.4) * mm, "end": v(-654.05, 914.4) * mm});
            skLineSegment(sketch, "E71.top", {"start": v(-635, 247.65) * mm, "end": v(-654.05, 247.65) * mm});
            skLineSegment(sketch, "E71.left", {"start": v(-635, 914.4) * mm, "end": v(-635, 247.65) * mm});
            skLineSegment(sketch, "E71.right", {"start": v(-654.05, 914.4) * mm, "end": v(-654.05, 247.65) * mm});
            skSolve(sketch);
        }
        {
            var Q0;
            Q0 = qSketchRegion(id + "F31", true);
            extrude(context, id + "F32", {"entities" : qUnion([Q0]), "depth" : 584.2 * mm, "offsetDistance" : 25.4 * mm});
        }
        {
            var Q0;
            Q0=makeQuery(id+"F13.opExtrude","CAP_FACE",FACE,{"disambiguationData":[OSD([sQuery(id+"F12.wireOp",EDGE,"E36.bottom"),sQuery(id+"F12.wireOp",EDGE,"E36.top"),sQuery(id+"F12.wireOp",EDGE,"E36.left"),sQuery(id+"F12.wireOp",EDGE,"E36.right")])],"isStart":false});
            var sketch = newSketch(context, id + "F33", { "sketchPlane" : qUnion([Q0])});
            skLineSegment(sketch, "E72.0", {"start": v(-3308.35, 247.65) * mm, "end": v(-3308.35, 914.4) * mm, "construction": true});
            skLineSegment(sketch, "E72.1", {"start": v(-2562.22, 247.65) * mm, "end": v(-2562.22, 914.4) * mm, "construction": true});
            skLineSegment(sketch, "E72.2", {"start": v(-1841.5, 914.4) * mm, "end": v(-3860.8, 914.4) * mm, "construction": true});
            skLineSegment(sketch, "E73.bottom", {"start": v(-3308.35, 914.4) * mm, "end": v(-3289.3, 914.4) * mm});
            skLineSegment(sketch, "E73.top", {"start": v(-3308.35, 247.65) * mm, "end": v(-3289.3, 247.65) * mm});
            skLineSegment(sketch, "E73.left", {"start": v(-3308.35, 914.4) * mm, "end": v(-3308.35, 247.65) * mm});
            skLineSegment(sketch, "E73.right", {"start": v(-3289.3, 914.4) * mm, "end": v(-3289.3, 247.65) * mm});
            skLineSegment(sketch, "E74.bottom", {"start": v(-2562.22, 914.4) * mm, "end": v(-2581.27, 914.4) * mm});
            skLineSegment(sketch, "E74.top", {"start": v(-2562.22, 247.65) * mm, "end": v(-2581.27, 247.65) * mm});
            skLineSegment(sketch, "E74.left", {"start": v(-2562.22, 914.4) * mm, "end": v(-2562.22, 247.65) * mm});
            skLineSegment(sketch, "E74.right", {"start": v(-2581.27, 914.4) * mm, "end": v(-2581.27, 247.65) * mm});
            skSolve(sketch);
        }
        {
            var Q0;
            Q0 = qSketchRegion(id + "F33", true);
            var Q1;
            Q1=makeQuery(id+"F32.opExtrude","CAP_FACE",FACE,{"disambiguationData":[OSD([sQuery(id+"F31.wireOp",EDGE,"E68.bottom"),sQuery(id+"F31.wireOp",EDGE,"E68.top"),sQuery(id+"F31.wireOp",EDGE,"E68.left"),sQuery(id+"F31.wireOp",EDGE,"E68.right")])],"isStart":false});
            extrude(context, id + "F34", {"entities" : qUnion([Q0]), "endBound" : BoundingType.UP_TO_SURFACE, "depth" : 25.4 * mm, "endBoundEntityFace" : qUnion([Q1]), "offsetDistance" : 25.4 * mm});
        }
        {
            var Q0;
            Q0=makeQuery(id+"F32.opExtrude","SWEPT_FACE",FACE,{"disambiguationData":[OSD([sQuery(id+"F31.wireOp",EDGE,"E64.right")])]});
            var sketch = newSketch(context, id + "F35", { "sketchPlane" : qUnion([Q0])});
            skLineSegment(sketch, "E75.bottom", {"start": v(914.4, 603.25) * mm, "end": v(895.35, 603.25) * mm});
            skLineSegment(sketch, "E75.top", {"start": v(914.4, 463.55) * mm, "end": v(895.35, 463.55) * mm});
            skLineSegment(sketch, "E75.left", {"start": v(914.4, 603.25) * mm, "end": v(914.4, 463.55) * mm});
            skLineSegment(sketch, "E75.right", {"start": v(895.35, 603.25) * mm, "end": v(895.35, 463.55) * mm});
            skLineSegment(sketch, "E76.bottom", {"start": v(247.65, 603.25) * mm, "end": v(387.35, 603.25) * mm});
            skLineSegment(sketch, "E76.top", {"start": v(247.65, 584.2) * mm, "end": v(387.35, 584.2) * mm});
            skLineSegment(sketch, "E76.left", {"start": v(247.65, 603.25) * mm, "end": v(247.65, 584.2) * mm});
            skLineSegment(sketch, "E76.right", {"start": v(387.35, 603.25) * mm, "end": v(387.35, 584.2) * mm});
            skLineSegment(sketch, "E77.bottom", {"start": v(247.65, 19.05) * mm, "end": v(266.7, 19.05) * mm});
            skLineSegment(sketch, "E77.top", {"start": v(247.65, 107.95) * mm, "end": v(266.7, 107.95) * mm});
            skLineSegment(sketch, "E77.left", {"start": v(247.65, 19.05) * mm, "end": v(247.65, 107.95) * mm});
            skLineSegment(sketch, "E77.right", {"start": v(266.7, 19.05) * mm, "end": v(266.7, 107.95) * mm});
            skLineSegment(sketch, "E78.bottom", {"start": v(914.4, 19.05) * mm, "end": v(895.35, 19.05) * mm});
            skLineSegment(sketch, "E78.top", {"start": v(914.4, 107.95) * mm, "end": v(895.35, 107.95) * mm});
            skLineSegment(sketch, "E78.left", {"start": v(914.4, 19.05) * mm, "end": v(914.4, 107.95) * mm});
            skLineSegment(sketch, "E78.right", {"start": v(895.35, 19.05) * mm, "end": v(895.35, 107.95) * mm});
            skSolve(sketch);
        }
        {
            var Q0;
            Q0 = qSketchRegion(id + "F35", true);
            var Q1;
            Q1=makeQuery(id+"F32.opExtrude","SWEPT_FACE",FACE,{"disambiguationData":[OSD([sQuery(id+"F31.wireOp",EDGE,"E68.left")])]});
            extrude(context, id + "F36", {"entities" : qUnion([Q0]), "endBound" : BoundingType.UP_TO_SURFACE, "depth" : 25.4 * mm, "endBoundEntityFace" : qUnion([Q1]), "offsetDistance" : 25.4 * mm});
        }
        {
            var Q0;
            Q0=makeQuery(id+"F34.opExtrude","SWEPT_FACE",FACE,{"disambiguationData":[OSD([sQuery(id+"F33.wireOp",EDGE,"E73.right")])]});
            var sketch = newSketch(context, id + "F37", { "sketchPlane" : qUnion([Q0])});
            skLineSegment(sketch, "E79.bottom", {"start": v(914.4, 603.25) * mm, "end": v(895.35, 603.25) * mm});
            skLineSegment(sketch, "E79.top", {"start": v(914.4, 463.55) * mm, "end": v(895.35, 463.55) * mm});
            skLineSegment(sketch, "E79.left", {"start": v(914.4, 603.25) * mm, "end": v(914.4, 463.55) * mm});
            skLineSegment(sketch, "E79.right", {"start": v(895.35, 603.25) * mm, "end": v(895.35, 463.55) * mm});
            skLineSegment(sketch, "E80.bottom", {"start": v(247.65, 603.25) * mm, "end": v(387.35, 603.25) * mm});
            skLineSegment(sketch, "E80.top", {"start": v(247.65, 584.2) * mm, "end": v(387.35, 584.2) * mm});
            skLineSegment(sketch, "E80.left", {"start": v(247.65, 603.25) * mm, "end": v(247.65, 584.2) * mm});
            skLineSegment(sketch, "E80.right", {"start": v(387.35, 603.25) * mm, "end": v(387.35, 584.2) * mm});
            skLineSegment(sketch, "E81.bottom", {"start": v(247.65, 19.05) * mm, "end": v(266.7, 19.05) * mm});
            skLineSegment(sketch, "E81.top", {"start": v(247.65, 107.95) * mm, "end": v(266.7, 107.95) * mm});
            skLineSegment(sketch, "E81.left", {"start": v(247.65, 19.05) * mm, "end": v(247.65, 107.95) * mm});
            skLineSegment(sketch, "E81.right", {"start": v(266.7, 19.05) * mm, "end": v(266.7, 107.95) * mm});
            skLineSegment(sketch, "E82.bottom", {"start": v(914.4, 19.05) * mm, "end": v(895.35, 19.05) * mm});
            skLineSegment(sketch, "E82.top", {"start": v(914.4, 107.95) * mm, "end": v(895.35, 107.95) * mm});
            skLineSegment(sketch, "E82.left", {"start": v(914.4, 19.05) * mm, "end": v(914.4, 107.95) * mm});
            skLineSegment(sketch, "E82.right", {"start": v(895.35, 19.05) * mm, "end": v(895.35, 107.95) * mm});
            skSolve(sketch);
        }
        {
            var Q0;
            Q0 = qSketchRegion(id + "F37", true);
            var Q1;
            Q1=makeQuery(id+"F34.opExtrude","SWEPT_FACE",FACE,{"disambiguationData":[OSD([sQuery(id+"F33.wireOp",EDGE,"E74.right")])]});
            extrude(context, id + "F38", {"entities" : qUnion([Q0]), "endBound" : BoundingType.UP_TO_SURFACE, "depth" : 25.4 * mm, "endBoundEntityFace" : qUnion([Q1]), "offsetDistance" : 25.4 * mm});
        }
        {
            var Q0;
            Q0=makeQuery(id+"F32.opExtrude","SWEPT_FACE",FACE,{"disambiguationData":[OSD([sQuery(id+"F31.wireOp",EDGE,"E67.left")])]});
            var sketch = newSketch(context, id + "F39", { "sketchPlane" : qUnion([Q0])});
            skLineSegment(sketch, "E83.0.0", {"start": v(387.35, 584.2) * mm, "end": v(387.35, 603.25) * mm});
            skLineSegment(sketch, "E83.0.1", {"start": v(387.35, 603.25) * mm, "end": v(247.65, 603.25) * mm});
            skLineSegment(sketch, "E83.0.2", {"start": v(247.65, 603.25) * mm, "end": v(247.65, 584.2) * mm});
            skLineSegment(sketch, "E83.0.3", {"start": v(247.65, 584.2) * mm, "end": v(387.35, 584.2) * mm});
            skLineSegment(sketch, "E83.1.0", {"start": v(247.65, 19.05) * mm, "end": v(266.7, 19.05) * mm});
            skLineSegment(sketch, "E83.1.1", {"start": v(266.7, 19.05) * mm, "end": v(266.7, 107.95) * mm});
            skLineSegment(sketch, "E83.1.2", {"start": v(266.7, 107.95) * mm, "end": v(247.65, 107.95) * mm});
            skLineSegment(sketch, "E83.1.3", {"start": v(247.65, 107.95) * mm, "end": v(247.65, 19.05) * mm});
            skLineSegment(sketch, "E83.2.0", {"start": v(914.4, 463.55) * mm, "end": v(914.4, 603.25) * mm});
            skLineSegment(sketch, "E83.2.1", {"start": v(914.4, 603.25) * mm, "end": v(895.35, 603.25) * mm});
            skLineSegment(sketch, "E83.2.2", {"start": v(895.35, 603.25) * mm, "end": v(895.35, 463.55) * mm});
            skLineSegment(sketch, "E83.2.3", {"start": v(895.35, 463.55) * mm, "end": v(914.4, 463.55) * mm});
            skLineSegment(sketch, "E83.3.0", {"start": v(895.35, 107.95) * mm, "end": v(895.35, 19.05) * mm});
            skLineSegment(sketch, "E83.3.1", {"start": v(895.35, 19.05) * mm, "end": v(914.4, 19.05) * mm});
            skLineSegment(sketch, "E83.3.2", {"start": v(914.4, 19.05) * mm, "end": v(914.4, 107.95) * mm});
            skLineSegment(sketch, "E83.3.3", {"start": v(914.4, 107.95) * mm, "end": v(895.35, 107.95) * mm});
            skSolve(sketch);
        }
        {
            var Q0;
            Q0 = qSketchRegion(id + "F39", true);
            var Q1;
            Q1=makeQuery(id+"F32.opExtrude","SWEPT_FACE",FACE,{"disambiguationData":[OSD([sQuery(id+"F31.wireOp",EDGE,"E63.left")])]});
            extrude(context, id + "F40", {"entities" : qUnion([Q0]), "endBound" : BoundingType.UP_TO_SURFACE, "depth" : 25.4 * mm, "endBoundEntityFace" : qUnion([Q1]), "offsetDistance" : 25.4 * mm});
        }
        {
            var Q0;
            Q0=makeQuery(id+"F32.opExtrude","SWEPT_FACE",FACE,{"disambiguationData":[OSD([sQuery(id+"F31.wireOp",EDGE,"E70.right")])]});
            var sketch = newSketch(context, id + "F41", { "sketchPlane" : qUnion([Q0])});
            skLineSegment(sketch, "E84.0.0", {"start": v(387.35, 603.25) * mm, "end": v(247.65, 603.25) * mm});
            skLineSegment(sketch, "E84.0.1", {"start": v(247.65, 603.25) * mm, "end": v(247.65, 584.2) * mm});
            skLineSegment(sketch, "E84.0.2", {"start": v(247.65, 584.2) * mm, "end": v(387.35, 584.2) * mm});
            skLineSegment(sketch, "E84.0.3", {"start": v(387.35, 584.2) * mm, "end": v(387.35, 603.25) * mm});
            skLineSegment(sketch, "E84.1.0", {"start": v(914.4, 603.25) * mm, "end": v(895.35, 603.25) * mm});
            skLineSegment(sketch, "E84.1.1", {"start": v(895.35, 603.25) * mm, "end": v(895.35, 463.55) * mm});
            skLineSegment(sketch, "E84.1.2", {"start": v(895.35, 463.55) * mm, "end": v(914.4, 463.55) * mm});
            skLineSegment(sketch, "E84.1.3", {"start": v(914.4, 463.55) * mm, "end": v(914.4, 603.25) * mm});
            skLineSegment(sketch, "E84.2.0", {"start": v(914.4, 19.05) * mm, "end": v(914.4, 107.95) * mm});
            skLineSegment(sketch, "E84.2.1", {"start": v(914.4, 107.95) * mm, "end": v(895.35, 107.95) * mm});
            skLineSegment(sketch, "E84.2.2", {"start": v(895.35, 107.95) * mm, "end": v(895.35, 19.05) * mm});
            skLineSegment(sketch, "E84.2.3", {"start": v(895.35, 19.05) * mm, "end": v(914.4, 19.05) * mm});
            skLineSegment(sketch, "E84.3.0", {"start": v(247.65, 19.05) * mm, "end": v(266.7, 19.05) * mm});
            skLineSegment(sketch, "E84.3.1", {"start": v(266.7, 19.05) * mm, "end": v(266.7, 107.95) * mm});
            skLineSegment(sketch, "E84.3.2", {"start": v(266.7, 107.95) * mm, "end": v(247.65, 107.95) * mm});
            skLineSegment(sketch, "E84.3.3", {"start": v(247.65, 107.95) * mm, "end": v(247.65, 19.05) * mm});
            skSolve(sketch);
        }
        {
            var Q0;
            Q0 = qSketchRegion(id + "F41", true);
            var Q1;
            Q1=makeQuery(id+"F32.opExtrude","SWEPT_FACE",FACE,{"disambiguationData":[OSD([sQuery(id+"F31.wireOp",EDGE,"E71.right")])]});
            extrude(context, id + "F42", {"entities" : qUnion([Q0]), "endBound" : BoundingType.UP_TO_SURFACE, "depth" : 25.4 * mm, "endBoundEntityFace" : qUnion([Q1]), "offsetDistance" : 25.4 * mm});
        }
        {
            var Q0;
            Q0=makeQuery(id+"F13.opExtrude","CAP_FACE",FACE,{"disambiguationData":[OSD([sQuery(id+"F12.wireOp",EDGE,"E36.bottom"),sQuery(id+"F12.wireOp",EDGE,"E36.top"),sQuery(id+"F12.wireOp",EDGE,"E36.left"),sQuery(id+"F12.wireOp",EDGE,"E36.right")])],"isStart":false});
            var sketch = newSketch(context, id + "F43", { "sketchPlane" : qUnion([Q0])});
            skLineSegment(sketch, "E85.0", {"start": v(-2028.82, 247.65) * mm, "end": v(-2009.77, 247.65) * mm, "construction": true});
            skLineSegment(sketch, "E86.bottom", {"start": v(-2009.77, 247.65) * mm, "end": v(-1841.5, 247.65) * mm});
            skLineSegment(sketch, "E86.top", {"start": v(-2009.77, 266.7) * mm, "end": v(-1841.5, 266.7) * mm});
            skLineSegment(sketch, "E86.left", {"start": v(-2009.77, 247.65) * mm, "end": v(-2009.77, 266.7) * mm});
            skLineSegment(sketch, "E86.right", {"start": v(-1841.5, 247.65) * mm, "end": v(-1841.5, 266.7) * mm});
            skLineSegment(sketch, "E87.0", {"start": v(-977.9, 247.65) * mm, "end": v(-958.85, 247.65) * mm, "construction": true});
            skLineSegment(sketch, "E88.0", {"start": v(-1206.5, 0) * mm, "end": v(-1206.5, 914.4) * mm, "construction": true});
            skLineSegment(sketch, "E88.1", {"start": v(-1841.5, 0) * mm, "end": v(-1841.5, 914.4) * mm, "construction": true});
            skLineSegment(sketch, "E89.bottom", {"start": v(-977.9, 247.65) * mm, "end": v(-1206.5, 247.65) * mm});
            skLineSegment(sketch, "E89.top", {"start": v(-977.9, 266.7) * mm, "end": v(-1206.5, 266.7) * mm});
            skLineSegment(sketch, "E89.left", {"start": v(-977.9, 247.65) * mm, "end": v(-977.9, 266.7) * mm});
            skLineSegment(sketch, "E89.right", {"start": v(-1206.5, 247.65) * mm, "end": v(-1206.5, 266.7) * mm});
            skSolve(sketch);
        }
        {
            var Q0;
            Q0 = qSketchRegion(id + "F43", true);
            var Q1;
            Q1=makeQuery(id+"F32.opExtrude","CAP_FACE",FACE,{"disambiguationData":[OSD([sQuery(id+"F31.wireOp",EDGE,"E70.bottom"),sQuery(id+"F31.wireOp",EDGE,"E70.top"),sQuery(id+"F31.wireOp",EDGE,"E70.left"),sQuery(id+"F31.wireOp",EDGE,"E70.right")])],"isStart":false});
            extrude(context, id + "F44", {"entities" : qUnion([Q0]), "endBound" : BoundingType.UP_TO_SURFACE, "depth" : 25.4 * mm, "endBoundEntityFace" : qUnion([Q1]), "offsetDistance" : 25.4 * mm});
        }
        {
            var Q0;
            Q0=makeQuery(id+"F32.opExtrude","SWEPT_FACE",FACE,{"disambiguationData":[OSD([sQuery(id+"F31.wireOp",EDGE,"E63.right")])]});
            var sketch = newSketch(context, id + "F45", { "sketchPlane" : qUnion([Q0])});
            skLineSegment(sketch, "E90.0", {"start": v(914.4, 603.25) * mm, "end": v(247.65, 603.25) * mm, "construction": true});
            skLineSegment(sketch, "E91.0", {"start": v(266.7, 603.25) * mm, "end": v(266.7, 19.05) * mm, "construction": true});
            skLineSegment(sketch, "E92.bottom", {"start": v(266.7, 603.25) * mm, "end": v(285.75, 603.25) * mm});
            skLineSegment(sketch, "E92.top", {"start": v(266.7, 539.75) * mm, "end": v(285.75, 539.75) * mm});
            skLineSegment(sketch, "E92.left", {"start": v(266.7, 603.25) * mm, "end": v(266.7, 539.75) * mm});
            skLineSegment(sketch, "E92.right", {"start": v(285.75, 603.25) * mm, "end": v(285.75, 539.75) * mm});
            skLineSegment(sketch, "E93.bottom", {"start": v(742.95, 603.25) * mm, "end": v(762, 603.25) * mm});
            skLineSegment(sketch, "E93.top", {"start": v(742.95, 539.75) * mm, "end": v(762, 539.75) * mm});
            skLineSegment(sketch, "E93.left", {"start": v(742.95, 603.25) * mm, "end": v(742.95, 539.75) * mm});
            skLineSegment(sketch, "E93.right", {"start": v(762, 603.25) * mm, "end": v(762, 539.75) * mm});
            skSolve(sketch);
        }
        {
            var Q0;
            Q0 = qSketchRegion(id + "F45", true);
            var Q1;
            Q1=makeQuery(id+"F32.opExtrude","SWEPT_FACE",FACE,{"disambiguationData":[OSD([sQuery(id+"F31.wireOp",EDGE,"E70.left")])]});
            extrude(context, id + "F46", {"entities" : qUnion([Q0]), "endBound" : BoundingType.UP_TO_SURFACE, "depth" : 25.4 * mm, "endBoundEntityFace" : qUnion([Q1]), "offsetDistance" : 25.4 * mm});
        }
        {
            var Q0;
            Q0=makeQuery(id+"F13.opExtrude","CAP_FACE",FACE,{"disambiguationData":[OSD([sQuery(id+"F12.wireOp",EDGE,"E36.bottom"),sQuery(id+"F12.wireOp",EDGE,"E36.top"),sQuery(id+"F12.wireOp",EDGE,"E36.left"),sQuery(id+"F12.wireOp",EDGE,"E36.right")])],"isStart":false});
            var sketch = newSketch(context, id + "F47", { "sketchPlane" : qUnion([Q0])});
            skLineSegment(sketch, "E94.0", {"start": v(-3860.8, 0) * mm, "end": v(-3860.8, 914.4) * mm, "construction": true});
            skLineSegment(sketch, "E94.1", {"start": v(-1841.5, 0) * mm, "end": v(-1841.5, 914.4) * mm, "construction": true});
            skLineSegment(sketch, "E94.2", {"start": v(-1206.5, 0) * mm, "end": v(-1206.5, 914.4) * mm, "construction": true});
            skLineSegment(sketch, "E94.3", {"start": v(0, 0) * mm, "end": v(0, 914.4) * mm, "construction": true});
            skLineSegment(sketch, "E95.0", {"start": v(-3327.4, 247.65) * mm, "end": v(-3841.75, 247.65) * mm, "construction": true});
            skLineSegment(sketch, "E95.1", {"start": v(-654.05, 247.65) * mm, "end": v(-958.85, 247.65) * mm, "construction": true});
            skLineSegment(sketch, "E96.0", {"start": v(-3860.8, 247.65) * mm, "end": v(-3841.75, 247.65) * mm, "construction": true});
            skLineSegment(sketch, "E97.bottom", {"start": v(-3860.8, 247.65) * mm, "end": v(-1841.5, 247.65) * mm});
            skLineSegment(sketch, "E97.top", {"start": v(-3860.8, 228.6) * mm, "end": v(-1841.5, 228.6) * mm});
            skLineSegment(sketch, "E97.left", {"start": v(-3860.8, 247.65) * mm, "end": v(-3860.8, 228.6) * mm});
            skLineSegment(sketch, "E97.right", {"start": v(-1841.5, 247.65) * mm, "end": v(-1841.5, 228.6) * mm});
            skLineSegment(sketch, "E98.0", {"start": v(-977.9, 247.65) * mm, "end": v(-1206.5, 247.65) * mm, "construction": true});
            skLineSegment(sketch, "E99.0", {"start": v(-635, 914.4) * mm, "end": v(-635, 247.65) * mm, "construction": true});
            skLineSegment(sketch, "E100.bottom", {"start": v(-1206.5, 247.65) * mm, "end": v(-635, 247.65) * mm});
            skLineSegment(sketch, "E100.top", {"start": v(-1206.5, 228.6) * mm, "end": v(-635, 228.6) * mm});
            skLineSegment(sketch, "E100.left", {"start": v(-1206.5, 247.65) * mm, "end": v(-1206.5, 228.6) * mm});
            skLineSegment(sketch, "E100.right", {"start": v(-635, 247.65) * mm, "end": v(-635, 228.6) * mm});
            skSolve(sketch);
        }
        {
            var Q0;
            Q0 = qSketchRegion(id + "F47", true);
            var Q1;
            Q1=makeQuery(id+"F40.opExtrude","SWEPT_FACE",FACE,{"disambiguationData":[OSD([sQuery(id+"F39.wireOp",EDGE,"E83.1.2")])]});
            extrude(context, id + "F48", {"entities" : qUnion([Q0]), "endBound" : BoundingType.UP_TO_SURFACE, "depth" : 25.4 * mm, "endBoundEntityFace" : qUnion([Q1]), "offsetDistance" : 25.4 * mm});
        }
        {
            var Q0;
            Q0=makeQuery(id+"F1.opExtrude","SWEPT_FACE",FACE,{"disambiguationData":[OSD([sQuery(id+"F0.wireOp",EDGE,"E3.bottom")])]});
            var sketch = newSketch(context, id + "F49", { "sketchPlane" : qUnion([Q0])});
            skLineSegment(sketch, "E101.0", {"start": v(-2228.85, -809.62) * mm, "end": v(-2228.85, 0) * mm, "construction": true});
            skLineSegment(sketch, "E101.1", {"start": v(-1860.55, -809.62) * mm, "end": v(-1860.55, 0) * mm, "construction": true});
            skLineSegment(sketch, "E101.3", {"start": v(-2228.85, -720.73) * mm, "end": v(-1860.55, -720.73) * mm, "construction": true});
            skLineSegment(sketch, "E102", {"start": v(-2228.85, -180.97) * mm, "end": v(-1860.55, -180.97) * mm, "construction": true});
            skLineSegment(sketch, "E103", {"start": v(-2228.85, -352.43) * mm, "end": v(-1860.55, -352.43) * mm, "construction": true});
            skLineSegment(sketch, "E104", {"start": v(-2228.85, -523.88) * mm, "end": v(-1860.55, -523.88) * mm, "construction": true});
            skLineSegment(sketch, "E105", {"start": v(-2228.85, -695.32) * mm, "end": v(-1860.55, -695.32) * mm, "construction": true});
            skLineSegment(sketch, "E106.bottom", {"start": v(-2228.85, -136.02) * mm, "end": v(-2216.15, -136.02) * mm});
            skLineSegment(sketch, "E106.top", {"start": v(-2228.85, -180.97) * mm, "end": v(-2216.15, -180.97) * mm});
            skLineSegment(sketch, "E106.left", {"start": v(-2228.85, -136.02) * mm, "end": v(-2228.85, -180.98) * mm});
            skLineSegment(sketch, "E106.right", {"start": v(-2216.15, -136.02) * mm, "end": v(-2216.15, -180.97) * mm});
            skLineSegment(sketch, "E107.bottom", {"start": v(-2228.85, -307.47) * mm, "end": v(-2216.15, -307.47) * mm});
            skLineSegment(sketch, "E107.top", {"start": v(-2228.85, -352.43) * mm, "end": v(-2216.15, -352.43) * mm});
            skLineSegment(sketch, "E107.left", {"start": v(-2228.85, -307.47) * mm, "end": v(-2228.85, -352.43) * mm});
            skLineSegment(sketch, "E107.right", {"start": v(-2216.15, -307.47) * mm, "end": v(-2216.15, -352.43) * mm});
            skLineSegment(sketch, "E108.bottom", {"start": v(-2228.85, -478.92) * mm, "end": v(-2216.15, -478.92) * mm});
            skLineSegment(sketch, "E108.top", {"start": v(-2228.85, -523.88) * mm, "end": v(-2216.15, -523.88) * mm});
            skLineSegment(sketch, "E108.left", {"start": v(-2228.85, -478.92) * mm, "end": v(-2228.85, -523.88) * mm});
            skLineSegment(sketch, "E108.right", {"start": v(-2216.15, -478.92) * mm, "end": v(-2216.15, -523.88) * mm});
            skLineSegment(sketch, "E109.bottom", {"start": v(-2228.85, -650.37) * mm, "end": v(-2216.15, -650.37) * mm});
            skLineSegment(sketch, "E109.top", {"start": v(-2228.85, -695.32) * mm, "end": v(-2216.15, -695.32) * mm});
            skLineSegment(sketch, "E109.left", {"start": v(-2228.85, -650.37) * mm, "end": v(-2228.85, -695.32) * mm});
            skLineSegment(sketch, "E109.right", {"start": v(-2216.15, -650.37) * mm, "end": v(-2216.15, -695.32) * mm});
            skLineSegment(sketch, "E110.0", {"start": v(-2228.85, 0) * mm, "end": v(-1860.55, 0) * mm, "construction": true});
            skLineSegment(sketch, "E111", {"start": v(-2044.7, 0) * mm, "end": v(-2044.7, -180.97) * mm, "construction": true});
            skLineSegment(sketch, "E112.MirrorCS", {"start": v(-1860.55, -136.02) * mm, "end": v(-1873.25, -136.02) * mm});
            skLineSegment(sketch, "E113.MirrorCS", {"start": v(-1860.55, -650.37) * mm, "end": v(-1873.25, -650.37) * mm});
            skLineSegment(sketch, "E114.MirrorCS", {"start": v(-1860.55, -307.47) * mm, "end": v(-1873.25, -307.47) * mm});
            skLineSegment(sketch, "E115.MirrorCS", {"start": v(-1860.55, -352.43) * mm, "end": v(-1873.25, -352.43) * mm});
            skLineSegment(sketch, "E116.MirrorCS", {"start": v(-1860.55, -523.88) * mm, "end": v(-1873.25, -523.88) * mm});
            skLineSegment(sketch, "E117.MirrorCS", {"start": v(-1860.55, -478.92) * mm, "end": v(-1873.25, -478.92) * mm});
            skLineSegment(sketch, "E118.MirrorCS", {"start": v(-1860.55, -695.32) * mm, "end": v(-1873.25, -695.32) * mm});
            skLineSegment(sketch, "E119.MirrorCS", {"start": v(-1860.55, -180.98) * mm, "end": v(-1873.25, -180.98) * mm});
            skLineSegment(sketch, "E120.MirrorCS", {"start": v(-1860.55, -307.47) * mm, "end": v(-1860.55, -352.42) * mm});
            skLineSegment(sketch, "E121.MirrorCS", {"start": v(-1860.55, -136.02) * mm, "end": v(-1860.55, -180.97) * mm});
            skLineSegment(sketch, "E122.MirrorCS", {"start": v(-1860.55, -650.37) * mm, "end": v(-1860.55, -695.32) * mm});
            skLineSegment(sketch, "E123.MirrorCS", {"start": v(-1860.55, -478.92) * mm, "end": v(-1860.55, -523.88) * mm});
            skLineSegment(sketch, "E124.MirrorCS", {"start": v(-1873.25, -478.92) * mm, "end": v(-1873.25, -523.88) * mm});
            skLineSegment(sketch, "E125.MirrorCS", {"start": v(-1873.25, -136.02) * mm, "end": v(-1873.25, -180.97) * mm});
            skLineSegment(sketch, "E126.MirrorCS", {"start": v(-1873.25, -307.47) * mm, "end": v(-1873.25, -352.42) * mm});
            skLineSegment(sketch, "E127.MirrorCS", {"start": v(-1873.25, -650.37) * mm, "end": v(-1873.25, -695.32) * mm});
            skLineSegment(sketch, "E128.0", {"start": v(-3841.75, -809.62) * mm, "end": v(-3841.75, 0) * mm, "construction": true});
            skLineSegment(sketch, "E128.1", {"start": v(-3841.75, -19.05) * mm, "end": v(-3282.95, -19.05) * mm, "construction": true});
            skLineSegment(sketch, "E128.2", {"start": v(-3282.95, -809.62) * mm, "end": v(-3282.95, 0) * mm, "construction": true});
            skLineSegment(sketch, "E128.3", {"start": v(-3841.75, -771.53) * mm, "end": v(-3282.95, -771.53) * mm, "construction": true});
            skLineSegment(sketch, "E129", {"start": v(-3841.75, -158.75) * mm, "end": v(-3282.95, -158.75) * mm, "construction": true});
            skLineSegment(sketch, "E130.bottom", {"start": v(-3841.75, -113.8) * mm, "end": v(-3829.05, -113.8) * mm});
            skLineSegment(sketch, "E130.top", {"start": v(-3841.75, -158.75) * mm, "end": v(-3829.05, -158.75) * mm});
            skLineSegment(sketch, "E130.left", {"start": v(-3841.75, -113.8) * mm, "end": v(-3841.75, -158.75) * mm});
            skLineSegment(sketch, "E130.right", {"start": v(-3829.05, -113.8) * mm, "end": v(-3829.05, -158.75) * mm});
            skLineSegment(sketch, "E131", {"start": v(-3562.35, -19.05) * mm, "end": v(-3562.35, -158.75) * mm, "construction": true});
            skLineSegment(sketch, "E132.MirrorCS", {"start": v(-3282.95, -113.8) * mm, "end": v(-3295.65, -113.8) * mm});
            skLineSegment(sketch, "E133.MirrorCS", {"start": v(-3282.95, -158.75) * mm, "end": v(-3295.65, -158.75) * mm});
            skLineSegment(sketch, "E134.MirrorCS", {"start": v(-3282.95, -113.8) * mm, "end": v(-3282.95, -158.75) * mm});
            skLineSegment(sketch, "E135.MirrorCS", {"start": v(-3295.65, -113.8) * mm, "end": v(-3295.65, -158.75) * mm});
            skLineSegment(sketch, "E136.0", {"start": v(-3244.85, -19.05) * mm, "end": v(-2876.55, -19.05) * mm, "construction": true});
            skLineSegment(sketch, "E136.2", {"start": v(-2876.55, -809.63) * mm, "end": v(-2876.55, 0) * mm, "construction": true});
            skLineSegment(sketch, "E136.3", {"start": v(-3244.85, -720.73) * mm, "end": v(-2876.55, -720.73) * mm, "construction": true});
            skLineSegment(sketch, "E137.bottom", {"start": v(-3244.85, -136.02) * mm, "end": v(-3232.15, -136.02) * mm});
            skLineSegment(sketch, "E137.top", {"start": v(-3244.85, -180.97) * mm, "end": v(-3232.15, -180.97) * mm});
            skLineSegment(sketch, "E137.left", {"start": v(-3244.85, -136.02) * mm, "end": v(-3244.85, -180.97) * mm});
            skLineSegment(sketch, "E137.right", {"start": v(-3232.15, -136.02) * mm, "end": v(-3232.15, -180.97) * mm});
            skLineSegment(sketch, "E138.bottom", {"start": v(-3244.85, -307.47) * mm, "end": v(-3232.15, -307.47) * mm});
            skLineSegment(sketch, "E138.top", {"start": v(-3244.85, -352.42) * mm, "end": v(-3232.15, -352.42) * mm});
            skLineSegment(sketch, "E138.left", {"start": v(-3244.85, -307.47) * mm, "end": v(-3244.85, -352.42) * mm});
            skLineSegment(sketch, "E138.right", {"start": v(-3232.15, -307.47) * mm, "end": v(-3232.15, -352.42) * mm});
            skLineSegment(sketch, "E139.bottom", {"start": v(-3244.85, -478.92) * mm, "end": v(-3232.15, -478.92) * mm});
            skLineSegment(sketch, "E139.top", {"start": v(-3244.85, -523.87) * mm, "end": v(-3232.15, -523.87) * mm});
            skLineSegment(sketch, "E139.left", {"start": v(-3244.85, -478.92) * mm, "end": v(-3244.85, -523.87) * mm});
            skLineSegment(sketch, "E139.right", {"start": v(-3232.15, -478.92) * mm, "end": v(-3232.15, -523.87) * mm});
            skLineSegment(sketch, "E140.bottom", {"start": v(-3244.85, -650.37) * mm, "end": v(-3232.15, -650.37) * mm});
            skLineSegment(sketch, "E140.top", {"start": v(-3244.85, -695.32) * mm, "end": v(-3232.15, -695.32) * mm});
            skLineSegment(sketch, "E140.left", {"start": v(-3244.85, -650.37) * mm, "end": v(-3244.85, -695.32) * mm});
            skLineSegment(sketch, "E140.right", {"start": v(-3232.15, -650.37) * mm, "end": v(-3232.15, -695.32) * mm});
            skLineSegment(sketch, "E141.MirrorCS", {"start": v(-2876.55, -136.02) * mm, "end": v(-2889.25, -136.02) * mm});
            skLineSegment(sketch, "E142.MirrorCS", {"start": v(-2876.55, -307.47) * mm, "end": v(-2889.25, -307.47) * mm});
            skLineSegment(sketch, "E143.MirrorCS", {"start": v(-2876.55, -695.32) * mm, "end": v(-2889.25, -695.32) * mm});
            skLineSegment(sketch, "E144.MirrorCS", {"start": v(-2876.55, -523.87) * mm, "end": v(-2889.25, -523.87) * mm});
            skLineSegment(sketch, "E145.MirrorCS", {"start": v(-2876.55, -180.97) * mm, "end": v(-2889.25, -180.97) * mm});
            skLineSegment(sketch, "E146.MirrorCS", {"start": v(-2876.55, -352.42) * mm, "end": v(-2889.25, -352.42) * mm});
            skLineSegment(sketch, "E147.MirrorCS", {"start": v(-2876.55, -478.92) * mm, "end": v(-2889.25, -478.92) * mm});
            skLineSegment(sketch, "E148.MirrorCS", {"start": v(-2876.55, -650.37) * mm, "end": v(-2889.25, -650.37) * mm});
            skLineSegment(sketch, "E149.MirrorCS", {"start": v(-2876.55, -307.47) * mm, "end": v(-2876.55, -352.42) * mm});
            skLineSegment(sketch, "E150.MirrorCS", {"start": v(-2876.55, -650.37) * mm, "end": v(-2876.55, -695.32) * mm});
            skLineSegment(sketch, "E151.MirrorCS", {"start": v(-2876.55, -136.02) * mm, "end": v(-2876.55, -180.97) * mm});
            skLineSegment(sketch, "E152.MirrorCS", {"start": v(-2876.55, -478.92) * mm, "end": v(-2876.55, -523.87) * mm});
            skLineSegment(sketch, "E153.MirrorCS", {"start": v(-2889.25, -307.47) * mm, "end": v(-2889.25, -352.42) * mm});
            skLineSegment(sketch, "E154.MirrorCS", {"start": v(-2889.25, -650.37) * mm, "end": v(-2889.25, -695.32) * mm});
            skLineSegment(sketch, "E155.MirrorCS", {"start": v(-2889.25, -478.92) * mm, "end": v(-2889.25, -523.87) * mm});
            skLineSegment(sketch, "E156.MirrorCS", {"start": v(-2889.25, -136.02) * mm, "end": v(-2889.25, -180.97) * mm});
            skLineSegment(sketch, "E157.1", {"start": v(-1187.45, 0) * mm, "end": v(-19.05, 0) * mm, "construction": true});
            skLineSegment(sketch, "E157.2", {"start": v(-19.05, -809.62) * mm, "end": v(-19.05, 0) * mm, "construction": true});
            skLineSegment(sketch, "E158.bottom", {"start": v(-1187.45, -237.1) * mm, "end": v(-1174.75, -237.1) * mm});
            skLineSegment(sketch, "E158.top", {"start": v(-1187.45, -282.07) * mm, "end": v(-1174.75, -282.07) * mm});
            skLineSegment(sketch, "E158.left", {"start": v(-1187.45, -237.1) * mm, "end": v(-1187.45, -282.07) * mm});
            skLineSegment(sketch, "E158.right", {"start": v(-1174.75, -237.1) * mm, "end": v(-1174.75, -282.07) * mm});
            skLineSegment(sketch, "E159.bottom", {"start": v(-1187.45, -364.62) * mm, "end": v(-1174.75, -364.62) * mm});
            skLineSegment(sketch, "E159.top", {"start": v(-1187.45, -409.58) * mm, "end": v(-1174.75, -409.58) * mm});
            skLineSegment(sketch, "E159.left", {"start": v(-1187.45, -364.62) * mm, "end": v(-1187.45, -409.58) * mm});
            skLineSegment(sketch, "E159.right", {"start": v(-1174.75, -364.62) * mm, "end": v(-1174.75, -409.58) * mm});
            skLineSegment(sketch, "E160.bottom", {"start": v(-1187.45, -522.86) * mm, "end": v(-1174.75, -522.86) * mm});
            skLineSegment(sketch, "E160.top", {"start": v(-1187.45, -567.82) * mm, "end": v(-1174.75, -567.82) * mm});
            skLineSegment(sketch, "E160.left", {"start": v(-1187.45, -522.86) * mm, "end": v(-1187.45, -567.82) * mm});
            skLineSegment(sketch, "E160.right", {"start": v(-1174.75, -522.86) * mm, "end": v(-1174.75, -567.82) * mm});
            skLineSegment(sketch, "E161.bottom", {"start": v(-1187.45, -650.37) * mm, "end": v(-1174.75, -650.37) * mm});
            skLineSegment(sketch, "E161.top", {"start": v(-1187.45, -695.32) * mm, "end": v(-1174.75, -695.32) * mm});
            skLineSegment(sketch, "E161.left", {"start": v(-1187.45, -650.37) * mm, "end": v(-1187.45, -695.32) * mm});
            skLineSegment(sketch, "E161.right", {"start": v(-1174.75, -650.37) * mm, "end": v(-1174.75, -695.32) * mm});
            skLineSegment(sketch, "E162", {"start": v(-603.25, 0) * mm, "end": v(-603.25, -679.45) * mm, "construction": true});
            skLineSegment(sketch, "E163.MirrorCS", {"start": v(-19.05, -650.37) * mm, "end": v(-31.75, -650.37) * mm});
            skLineSegment(sketch, "E164.MirrorCS", {"start": v(-19.05, -364.62) * mm, "end": v(-31.75, -364.62) * mm});
            skLineSegment(sketch, "E165.MirrorCS", {"start": v(-31.75, -522.86) * mm, "end": v(-31.75, -567.82) * mm});
            skLineSegment(sketch, "E166.MirrorCS", {"start": v(-31.75, -364.62) * mm, "end": v(-31.75, -409.57) * mm});
            skLineSegment(sketch, "E167.MirrorCS", {"start": v(-19.05, -409.57) * mm, "end": v(-31.75, -409.57) * mm});
            skLineSegment(sketch, "E168.MirrorCS", {"start": v(-19.05, -237.1) * mm, "end": v(-19.05, -282.07) * mm});
            skLineSegment(sketch, "E169.MirrorCS", {"start": v(-19.05, -567.82) * mm, "end": v(-31.75, -567.82) * mm});
            skLineSegment(sketch, "E170.MirrorCS", {"start": v(-31.75, -237.1) * mm, "end": v(-31.75, -282.07) * mm});
            skLineSegment(sketch, "E171.MirrorCS", {"start": v(-19.05, -237.1) * mm, "end": v(-31.75, -237.1) * mm});
            skLineSegment(sketch, "E172.MirrorCS", {"start": v(-19.05, -364.62) * mm, "end": v(-19.05, -409.57) * mm});
            skLineSegment(sketch, "E173.MirrorCS", {"start": v(-31.75, -650.37) * mm, "end": v(-31.75, -695.32) * mm});
            skLineSegment(sketch, "E174.MirrorCS", {"start": v(-19.05, -650.37) * mm, "end": v(-19.05, -695.32) * mm});
            skLineSegment(sketch, "E175.MirrorCS", {"start": v(-19.05, -695.32) * mm, "end": v(-31.75, -695.32) * mm});
            skLineSegment(sketch, "E176.MirrorCS", {"start": v(-19.05, -282.07) * mm, "end": v(-31.75, -282.07) * mm});
            skLineSegment(sketch, "E177.MirrorCS", {"start": v(-19.05, -522.86) * mm, "end": v(-31.75, -522.86) * mm});
            skLineSegment(sketch, "E178.MirrorCS", {"start": v(-19.05, -522.86) * mm, "end": v(-19.05, -567.82) * mm});
            skLineSegment(sketch, "E179.bottom", {"start": v(-2216.15, -555.62) * mm, "end": v(-2203.45, -555.62) * mm, "construction": true});
            skLineSegment(sketch, "E179.top", {"start": v(-2216.15, -714.38) * mm, "end": v(-2203.45, -714.38) * mm, "construction": true});
            skLineSegment(sketch, "E179.left", {"start": v(-2216.15, -555.62) * mm, "end": v(-2216.15, -714.38) * mm, "construction": true});
            skLineSegment(sketch, "E179.right", {"start": v(-2203.45, -555.62) * mm, "end": v(-2203.45, -714.38) * mm, "construction": true});
            skLineSegment(sketch, "E180.bottom", {"start": v(-2216.15, -384.18) * mm, "end": v(-2203.45, -384.18) * mm, "construction": true});
            skLineSegment(sketch, "E180.top", {"start": v(-2216.15, -542.92) * mm, "end": v(-2203.45, -542.92) * mm, "construction": true});
            skLineSegment(sketch, "E180.left", {"start": v(-2216.15, -384.18) * mm, "end": v(-2216.15, -542.92) * mm, "construction": true});
            skLineSegment(sketch, "E180.right", {"start": v(-2203.45, -384.18) * mm, "end": v(-2203.45, -542.92) * mm, "construction": true});
            skLineSegment(sketch, "E181.bottom", {"start": v(-2216.15, -212.72) * mm, "end": v(-2203.45, -212.72) * mm, "construction": true});
            skLineSegment(sketch, "E181.top", {"start": v(-2216.15, -371.48) * mm, "end": v(-2203.45, -371.48) * mm, "construction": true});
            skLineSegment(sketch, "E181.left", {"start": v(-2216.15, -212.72) * mm, "end": v(-2216.15, -371.48) * mm, "construction": true});
            skLineSegment(sketch, "E181.right", {"start": v(-2203.45, -212.72) * mm, "end": v(-2203.45, -371.48) * mm, "construction": true});
            skLineSegment(sketch, "E182.bottom", {"start": v(-2216.15, -41.27) * mm, "end": v(-2203.45, -41.27) * mm, "construction": true});
            skLineSegment(sketch, "E182.top", {"start": v(-2216.15, -200.03) * mm, "end": v(-2203.45, -200.03) * mm, "construction": true});
            skLineSegment(sketch, "E182.left", {"start": v(-2216.15, -41.27) * mm, "end": v(-2216.15, -200.03) * mm, "construction": true});
            skLineSegment(sketch, "E182.right", {"start": v(-2203.45, -41.28) * mm, "end": v(-2203.45, -200.03) * mm, "construction": true});
            skLineSegment(sketch, "E183.bottom", {"start": v(-1174.75, -441.32) * mm, "end": v(-1162.05, -441.32) * mm, "construction": true});
            skLineSegment(sketch, "E183.top", {"start": v(-1174.75, -714.38) * mm, "end": v(-1162.05, -714.38) * mm, "construction": true});
            skLineSegment(sketch, "E183.left", {"start": v(-1174.75, -441.32) * mm, "end": v(-1174.75, -714.38) * mm, "construction": true});
            skLineSegment(sketch, "E183.right", {"start": v(-1162.05, -441.32) * mm, "end": v(-1162.05, -714.38) * mm, "construction": true});
            skSolve(sketch);
        }
        {
            var Q0;
            Q0 = qSketchRegion(id + "F49", true);
            extrude(context, id + "F50", {"entities" : qUnion([Q0]), "oppositeDirection" : true, "depth" : 596.9 * mm, "offsetDistance" : 25.4 * mm});
        }
        {
            var Q0;
            Q0=makeQuery(id+"F1.opExtrude","SWEPT_FACE",FACE,{"disambiguationData":[OSD([sQuery(id+"F0.wireOp",EDGE,"E2.bottom")])]});
            var sketch = newSketch(context, id + "F51", { "sketchPlane" : qUnion([Q0])});
            skLineSegment(sketch, "E184.1", {"start": v(-3841.75, -809.62) * mm, "end": v(-3841.75, 0) * mm, "construction": true});
            skLineSegment(sketch, "E184.2", {"start": v(-3282.95, -809.62) * mm, "end": v(-3282.95, 0) * mm, "construction": true});
            skLineSegment(sketch, "E184.3", {"start": v(-3841.75, -771.53) * mm, "end": v(-3282.95, -771.53) * mm, "construction": true});
            skLineSegment(sketch, "E185.0", {"start": v(-3841.75, 0) * mm, "end": v(-3282.95, 0) * mm, "construction": true});
            skLineSegment(sketch, "E186.bottom", {"start": v(-3841.75, -720.22) * mm, "end": v(-3829.05, -720.22) * mm});
            skLineSegment(sketch, "E186.top", {"start": v(-3841.75, -765.18) * mm, "end": v(-3829.05, -765.18) * mm});
            skLineSegment(sketch, "E186.left", {"start": v(-3841.75, -720.22) * mm, "end": v(-3841.75, -765.18) * mm});
            skLineSegment(sketch, "E186.right", {"start": v(-3829.05, -720.22) * mm, "end": v(-3829.05, -765.18) * mm});
            skLineSegment(sketch, "E187", {"start": v(-3562.35, 0) * mm, "end": v(-3562.35, -736.6) * mm, "construction": true});
            skLineSegment(sketch, "E188.MirrorCS", {"start": v(-3295.65, -720.22) * mm, "end": v(-3295.65, -765.18) * mm});
            skLineSegment(sketch, "E189.MirrorCS", {"start": v(-3282.95, -720.22) * mm, "end": v(-3295.65, -720.22) * mm});
            skLineSegment(sketch, "E190.MirrorCS", {"start": v(-3282.95, -765.18) * mm, "end": v(-3295.65, -765.18) * mm});
            skLineSegment(sketch, "E191.MirrorCS", {"start": v(-3282.95, -720.22) * mm, "end": v(-3282.95, -765.18) * mm});
            skSolve(sketch);
        }
        {
            var Q0;
            Q0 = qSketchRegion(id + "F51", true);
            extrude(context, id + "F52", {"entities" : qUnion([Q0]), "oppositeDirection" : true, "depth" : 647.7 * mm, "offsetDistance" : 25.4 * mm});
        }
        {
            var Q0;
            Q0=makeQuery(id+"F32.opExtrude","SWEPT_FACE",FACE,{"disambiguationData":[OSD([sQuery(id+"F31.wireOp",EDGE,"E63.top")])]});
            var sketch = newSketch(context, id + "F53", { "sketchPlane" : qUnion([Q0])});
            skLineSegment(sketch, "E192.0", {"start": v(-1841.5, 19.05) * mm, "end": v(-3860.8, 19.05) * mm, "construction": true});
            skLineSegment(sketch, "E192.1", {"start": v(-3841.75, 603.25) * mm, "end": v(-3841.75, 19.05) * mm, "construction": true});
            skLineSegment(sketch, "E192.2", {"start": v(-3327.4, 603.25) * mm, "end": v(-3327.4, 19.05) * mm, "construction": true});
            skLineSegment(sketch, "E192.3", {"start": v(-3289.3, 603.25) * mm, "end": v(-3289.3, 19.05) * mm, "construction": true});
            skLineSegment(sketch, "E192.4", {"start": v(-2581.27, 603.25) * mm, "end": v(-2581.27, 19.05) * mm, "construction": true});
            skLineSegment(sketch, "E192.5", {"start": v(-2543.17, 603.25) * mm, "end": v(-2543.17, 19.05) * mm, "construction": true});
            skLineSegment(sketch, "E192.6", {"start": v(-2028.82, 603.25) * mm, "end": v(-2028.82, 19.05) * mm, "construction": true});
            skLineSegment(sketch, "E192.7", {"start": v(-958.85, 603.25) * mm, "end": v(-958.85, 19.05) * mm, "construction": true});
            skLineSegment(sketch, "E192.8", {"start": v(-654.05, 603.25) * mm, "end": v(-654.05, 19.05) * mm, "construction": true});
            skLineSegment(sketch, "E193", {"start": v(-3841.75, 133.35) * mm, "end": v(-654.05, 133.35) * mm, "construction": true});
            skLineSegment(sketch, "E194", {"start": v(-3841.75, 304.8) * mm, "end": v(-654.05, 304.8) * mm, "construction": true});
            skLineSegment(sketch, "E195", {"start": v(-3841.75, 476.25) * mm, "end": v(-654.05, 476.25) * mm, "construction": true});
            skLineSegment(sketch, "E196.bottom", {"start": v(-3841.75, 521.2) * mm, "end": v(-3829.05, 521.2) * mm});
            skLineSegment(sketch, "E196.top", {"start": v(-3841.75, 476.25) * mm, "end": v(-3829.05, 476.25) * mm});
            skLineSegment(sketch, "E196.left", {"start": v(-3841.75, 521.2) * mm, "end": v(-3841.75, 476.25) * mm});
            skLineSegment(sketch, "E196.right", {"start": v(-3829.05, 521.2) * mm, "end": v(-3829.05, 476.25) * mm});
            skPoint(sketch, "E197", {"position": v(-3289.3, 476.25) * mm});
            skLineSegment(sketch, "E198.bottom", {"start": v(-3289.3, 521.2) * mm, "end": v(-3276.6, 521.2) * mm});
            skLineSegment(sketch, "E198.top", {"start": v(-3289.3, 476.25) * mm, "end": v(-3276.6, 476.25) * mm});
            skLineSegment(sketch, "E198.left", {"start": v(-3289.3, 521.2) * mm, "end": v(-3289.3, 476.25) * mm});
            skLineSegment(sketch, "E198.right", {"start": v(-3276.6, 521.2) * mm, "end": v(-3276.6, 476.25) * mm});
            skLineSegment(sketch, "E199.bottom", {"start": v(-3841.75, 349.76) * mm, "end": v(-3829.05, 349.76) * mm});
            skLineSegment(sketch, "E199.top", {"start": v(-3841.75, 304.8) * mm, "end": v(-3829.05, 304.8) * mm});
            skLineSegment(sketch, "E199.left", {"start": v(-3841.75, 349.76) * mm, "end": v(-3841.75, 304.8) * mm});
            skLineSegment(sketch, "E199.right", {"start": v(-3829.05, 349.76) * mm, "end": v(-3829.05, 304.8) * mm});
            skLineSegment(sketch, "E200.bottom", {"start": v(-3841.75, 178.3) * mm, "end": v(-3829.05, 178.3) * mm});
            skLineSegment(sketch, "E200.top", {"start": v(-3841.75, 133.35) * mm, "end": v(-3829.05, 133.35) * mm});
            skLineSegment(sketch, "E200.left", {"start": v(-3841.75, 178.3) * mm, "end": v(-3841.75, 133.35) * mm});
            skLineSegment(sketch, "E200.right", {"start": v(-3829.05, 178.3) * mm, "end": v(-3829.05, 133.35) * mm});
            skPoint(sketch, "E201", {"position": v(-3289.3, 304.8) * mm});
            skPoint(sketch, "E202", {"position": v(-3289.3, 133.35) * mm});
            skPoint(sketch, "E203", {"position": v(-2543.17, 476.25) * mm});
            skPoint(sketch, "E204", {"position": v(-2543.17, 304.8) * mm});
            skPoint(sketch, "E205", {"position": v(-2543.17, 133.35) * mm});
            skPoint(sketch, "E206", {"position": v(-958.85, 476.25) * mm});
            skPoint(sketch, "E207", {"position": v(-958.85, 304.8) * mm});
            skPoint(sketch, "E208", {"position": v(-958.85, 133.35) * mm});
            skLineSegment(sketch, "E209.bottom", {"start": v(-3289.3, 178.3) * mm, "end": v(-3276.6, 178.3) * mm});
            skLineSegment(sketch, "E209.top", {"start": v(-3289.3, 133.35) * mm, "end": v(-3276.6, 133.35) * mm});
            skLineSegment(sketch, "E209.left", {"start": v(-3289.3, 178.3) * mm, "end": v(-3289.3, 133.35) * mm});
            skLineSegment(sketch, "E209.right", {"start": v(-3276.6, 178.3) * mm, "end": v(-3276.6, 133.35) * mm});
            skLineSegment(sketch, "E210.bottom", {"start": v(-3289.3, 349.76) * mm, "end": v(-3276.6, 349.76) * mm});
            skLineSegment(sketch, "E210.top", {"start": v(-3289.3, 304.8) * mm, "end": v(-3276.6, 304.8) * mm});
            skLineSegment(sketch, "E210.left", {"start": v(-3289.3, 349.76) * mm, "end": v(-3289.3, 304.8) * mm});
            skLineSegment(sketch, "E210.right", {"start": v(-3276.6, 349.76) * mm, "end": v(-3276.6, 304.8) * mm});
            skLineSegment(sketch, "E211.bottom", {"start": v(-2543.17, 178.3) * mm, "end": v(-2530.47, 178.3) * mm});
            skLineSegment(sketch, "E211.top", {"start": v(-2543.17, 133.35) * mm, "end": v(-2530.47, 133.35) * mm});
            skLineSegment(sketch, "E211.left", {"start": v(-2543.17, 178.3) * mm, "end": v(-2543.17, 133.35) * mm});
            skLineSegment(sketch, "E211.right", {"start": v(-2530.47, 178.3) * mm, "end": v(-2530.47, 133.35) * mm});
            skLineSegment(sketch, "E212.bottom", {"start": v(-2543.17, 521.2) * mm, "end": v(-2530.47, 521.2) * mm});
            skLineSegment(sketch, "E212.top", {"start": v(-2543.17, 476.25) * mm, "end": v(-2530.47, 476.25) * mm});
            skLineSegment(sketch, "E212.left", {"start": v(-2543.17, 521.2) * mm, "end": v(-2543.17, 476.25) * mm});
            skLineSegment(sketch, "E212.right", {"start": v(-2530.47, 521.2) * mm, "end": v(-2530.47, 476.25) * mm});
            skLineSegment(sketch, "E213.bottom", {"start": v(-2543.17, 349.76) * mm, "end": v(-2530.47, 349.76) * mm});
            skLineSegment(sketch, "E213.top", {"start": v(-2543.17, 304.8) * mm, "end": v(-2530.47, 304.8) * mm});
            skLineSegment(sketch, "E213.left", {"start": v(-2543.17, 349.76) * mm, "end": v(-2543.17, 304.8) * mm});
            skLineSegment(sketch, "E213.right", {"start": v(-2530.47, 349.76) * mm, "end": v(-2530.47, 304.8) * mm});
            skLineSegment(sketch, "E214.bottom", {"start": v(-958.85, 178.3) * mm, "end": v(-946.15, 178.3) * mm});
            skLineSegment(sketch, "E214.top", {"start": v(-958.85, 133.35) * mm, "end": v(-946.15, 133.35) * mm});
            skLineSegment(sketch, "E214.left", {"start": v(-958.85, 178.3) * mm, "end": v(-958.85, 133.35) * mm});
            skLineSegment(sketch, "E214.right", {"start": v(-946.15, 178.3) * mm, "end": v(-946.15, 133.35) * mm});
            skLineSegment(sketch, "E215.bottom", {"start": v(-958.85, 349.76) * mm, "end": v(-946.15, 349.76) * mm});
            skLineSegment(sketch, "E215.top", {"start": v(-958.85, 304.8) * mm, "end": v(-946.15, 304.8) * mm});
            skLineSegment(sketch, "E215.left", {"start": v(-958.85, 349.76) * mm, "end": v(-958.85, 304.8) * mm});
            skLineSegment(sketch, "E215.right", {"start": v(-946.15, 349.76) * mm, "end": v(-946.15, 304.8) * mm});
            skLineSegment(sketch, "E216.bottom", {"start": v(-958.85, 521.2) * mm, "end": v(-946.15, 521.2) * mm});
            skLineSegment(sketch, "E216.top", {"start": v(-958.85, 476.25) * mm, "end": v(-946.15, 476.25) * mm});
            skLineSegment(sketch, "E216.left", {"start": v(-958.85, 521.2) * mm, "end": v(-958.85, 476.25) * mm});
            skLineSegment(sketch, "E216.right", {"start": v(-946.15, 521.2) * mm, "end": v(-946.15, 476.25) * mm});
            skLineSegment(sketch, "E217.0", {"start": v(-3327.4, 603.25) * mm, "end": v(-3841.75, 603.25) * mm, "construction": true});
            skLineSegment(sketch, "E217.1", {"start": v(-2581.27, 603.25) * mm, "end": v(-3289.3, 603.25) * mm, "construction": true});
            skLineSegment(sketch, "E217.2", {"start": v(-2028.82, 603.25) * mm, "end": v(-2543.18, 603.25) * mm, "construction": true});
            skLineSegment(sketch, "E217.3", {"start": v(-654.05, 603.25) * mm, "end": v(-958.85, 603.25) * mm, "construction": true});
            skLineSegment(sketch, "E218", {"start": v(-3584.57, 603.25) * mm, "end": v(-3584.57, 133.35) * mm, "construction": true});
            skLineSegment(sketch, "E219", {"start": v(-2935.29, 603.25) * mm, "end": v(-2935.29, 133.35) * mm, "construction": true});
            skLineSegment(sketch, "E220", {"start": v(-2286, 603.25) * mm, "end": v(-2286, 133.35) * mm, "construction": true});
            skLineSegment(sketch, "E221", {"start": v(-806.45, 603.25) * mm, "end": v(-806.45, 133.35) * mm, "construction": true});
            skLineSegment(sketch, "E222.MirrorCS", {"start": v(-3327.4, 476.25) * mm, "end": v(-3340.1, 476.25) * mm});
            skLineSegment(sketch, "E223.MirrorCS", {"start": v(-3327.4, 178.3) * mm, "end": v(-3340.1, 178.3) * mm});
            skLineSegment(sketch, "E224.MirrorCS", {"start": v(-3327.4, 304.8) * mm, "end": v(-3340.1, 304.8) * mm});
            skLineSegment(sketch, "E225.MirrorCS", {"start": v(-3327.4, 178.3) * mm, "end": v(-3327.4, 133.35) * mm});
            skLineSegment(sketch, "E226.MirrorCS", {"start": v(-3327.4, 521.2) * mm, "end": v(-3340.1, 521.2) * mm});
            skLineSegment(sketch, "E227.MirrorCS", {"start": v(-3340.1, 178.3) * mm, "end": v(-3340.1, 133.35) * mm});
            skLineSegment(sketch, "E228.MirrorCS", {"start": v(-3327.4, 521.2) * mm, "end": v(-3327.4, 476.25) * mm});
            skLineSegment(sketch, "E229.MirrorCS", {"start": v(-3327.4, 349.76) * mm, "end": v(-3340.1, 349.76) * mm});
            skLineSegment(sketch, "E230.MirrorCS", {"start": v(-3327.4, 133.35) * mm, "end": v(-3340.1, 133.35) * mm});
            skLineSegment(sketch, "E231.MirrorCS", {"start": v(-3340.1, 349.76) * mm, "end": v(-3340.1, 304.8) * mm});
            skLineSegment(sketch, "E232.MirrorCS", {"start": v(-3327.4, 349.76) * mm, "end": v(-3327.4, 304.8) * mm});
            skLineSegment(sketch, "E233.MirrorCS", {"start": v(-3340.1, 521.2) * mm, "end": v(-3340.1, 476.25) * mm});
            skLineSegment(sketch, "E234.MirrorCS", {"start": v(-2581.27, 178.3) * mm, "end": v(-2593.97, 178.3) * mm});
            skLineSegment(sketch, "E235.MirrorCS", {"start": v(-2581.27, 304.8) * mm, "end": v(-2593.97, 304.8) * mm});
            skLineSegment(sketch, "E236.MirrorCS", {"start": v(-2581.27, 349.76) * mm, "end": v(-2593.97, 349.76) * mm});
            skLineSegment(sketch, "E237.MirrorCS", {"start": v(-2581.27, 476.25) * mm, "end": v(-2593.97, 476.25) * mm});
            skLineSegment(sketch, "E238.MirrorCS", {"start": v(-2581.27, 521.2) * mm, "end": v(-2593.97, 521.2) * mm});
            skLineSegment(sketch, "E239.MirrorCS", {"start": v(-2581.27, 133.35) * mm, "end": v(-2593.97, 133.35) * mm});
            skPoint(sketch, "E240.MirrorP", {"position": v(-2581.27, 304.8) * mm});
            skPoint(sketch, "E241.MirrorP", {"position": v(-2581.27, 476.25) * mm});
            skPoint(sketch, "E242.MirrorP", {"position": v(-2581.27, 133.35) * mm});
            skLineSegment(sketch, "E243.MirrorCS", {"start": v(-2593.97, 521.2) * mm, "end": v(-2593.97, 476.25) * mm});
            skLineSegment(sketch, "E244.MirrorCS", {"start": v(-2581.27, 521.2) * mm, "end": v(-2581.27, 476.25) * mm});
            skLineSegment(sketch, "E245.MirrorCS", {"start": v(-2593.97, 349.76) * mm, "end": v(-2593.97, 304.8) * mm});
            skLineSegment(sketch, "E246.MirrorCS", {"start": v(-2593.97, 178.3) * mm, "end": v(-2593.97, 133.35) * mm});
            skLineSegment(sketch, "E247.MirrorCS", {"start": v(-2581.27, 349.76) * mm, "end": v(-2581.27, 304.8) * mm});
            skLineSegment(sketch, "E248.MirrorCS", {"start": v(-2581.27, 178.3) * mm, "end": v(-2581.27, 133.35) * mm});
            skLineSegment(sketch, "E249.MirrorCS", {"start": v(-2028.82, 349.76) * mm, "end": v(-2041.52, 349.76) * mm});
            skLineSegment(sketch, "E250.MirrorCS", {"start": v(-2028.82, 521.2) * mm, "end": v(-2041.52, 521.2) * mm});
            skLineSegment(sketch, "E251.MirrorCS", {"start": v(-2028.83, 521.2) * mm, "end": v(-2028.83, 476.25) * mm});
            skLineSegment(sketch, "E252.MirrorCS", {"start": v(-2028.82, 133.35) * mm, "end": v(-2041.52, 133.35) * mm});
            skLineSegment(sketch, "E253.MirrorCS", {"start": v(-2028.83, 349.76) * mm, "end": v(-2028.83, 304.8) * mm});
            skLineSegment(sketch, "E254.MirrorCS", {"start": v(-2041.53, 349.76) * mm, "end": v(-2041.53, 304.8) * mm});
            skLineSegment(sketch, "E255.MirrorCS", {"start": v(-2041.53, 521.2) * mm, "end": v(-2041.53, 476.25) * mm});
            skLineSegment(sketch, "E256.MirrorCS", {"start": v(-2028.82, 476.25) * mm, "end": v(-2041.52, 476.25) * mm});
            skLineSegment(sketch, "E257.MirrorCS", {"start": v(-2028.82, 304.8) * mm, "end": v(-2041.52, 304.8) * mm});
            skLineSegment(sketch, "E258.MirrorCS", {"start": v(-2028.82, 178.3) * mm, "end": v(-2041.52, 178.3) * mm});
            skLineSegment(sketch, "E259.MirrorCS", {"start": v(-2041.53, 178.3) * mm, "end": v(-2041.53, 133.35) * mm});
            skLineSegment(sketch, "E260.MirrorCS", {"start": v(-2028.83, 178.3) * mm, "end": v(-2028.83, 133.35) * mm});
            skPoint(sketch, "E261.MirrorP", {"position": v(-2028.83, 133.35) * mm});
            skPoint(sketch, "E262.MirrorP", {"position": v(-2028.83, 476.25) * mm});
            skPoint(sketch, "E263.MirrorP", {"position": v(-2028.83, 304.8) * mm});
            skLineSegment(sketch, "E264.MirrorCS", {"start": v(-654.05, 133.35) * mm, "end": v(-666.75, 133.35) * mm});
            skLineSegment(sketch, "E265.MirrorCS", {"start": v(-666.75, 521.2) * mm, "end": v(-666.75, 476.25) * mm});
            skLineSegment(sketch, "E266.MirrorCS", {"start": v(-654.05, 476.25) * mm, "end": v(-666.75, 476.25) * mm});
            skLineSegment(sketch, "E267.MirrorCS", {"start": v(-654.05, 304.8) * mm, "end": v(-666.75, 304.8) * mm});
            skLineSegment(sketch, "E268.MirrorCS", {"start": v(-654.05, 521.2) * mm, "end": v(-654.05, 476.25) * mm});
            skLineSegment(sketch, "E269.MirrorCS", {"start": v(-654.05, 349.76) * mm, "end": v(-666.75, 349.76) * mm});
            skLineSegment(sketch, "E270.MirrorCS", {"start": v(-654.05, 178.3) * mm, "end": v(-666.75, 178.3) * mm});
            skLineSegment(sketch, "E271.MirrorCS", {"start": v(-654.05, 521.2) * mm, "end": v(-666.75, 521.2) * mm});
            skLineSegment(sketch, "E272.MirrorCS", {"start": v(-666.75, 349.76) * mm, "end": v(-666.75, 304.8) * mm});
            skLineSegment(sketch, "E273.MirrorCS", {"start": v(-654.05, 349.76) * mm, "end": v(-654.05, 304.8) * mm});
            skLineSegment(sketch, "E274.MirrorCS", {"start": v(-666.75, 178.3) * mm, "end": v(-666.75, 133.35) * mm});
            skLineSegment(sketch, "E275.MirrorCS", {"start": v(-654.05, 178.3) * mm, "end": v(-654.05, 133.35) * mm});
            skPoint(sketch, "E276.MirrorP", {"position": v(-654.05, 304.8) * mm});
            skPoint(sketch, "E277.MirrorP", {"position": v(-654.05, 133.35) * mm});
            skPoint(sketch, "E278.MirrorP", {"position": v(-654.05, 476.25) * mm});
            skSolve(sketch);
        }
        {
            var Q0;
            Q0 = qSketchRegion(id + "F53", true);
            extrude(context, id + "F54", {"entities" : qUnion([Q0]), "oppositeDirection" : true, "depth" : 596.9 * mm, "offsetDistance" : 25.4 * mm});
        }
        {
            var Q0;
            Q0=makeQuery(id+"F9.opExtrude","SWEPT_FACE",FACE,{"disambiguationData":[OSD([sQuery(id+"F8.wireOp",EDGE,"E27.right")])]});
            var sketch = newSketch(context, id + "F55", { "sketchPlane" : qUnion([Q0])});
            skLineSegment(sketch, "E279.0", {"start": v(-3841.75, -771.53) * mm, "end": v(-3841.75, -809.62) * mm, "construction": true});
            skLineSegment(sketch, "E279.1", {"start": v(-3841.75, -809.62) * mm, "end": v(-3282.95, -809.62) * mm, "construction": true});
            skLineSegment(sketch, "E280.bottom", {"start": v(-3841.75, -809.62) * mm, "end": v(-3803.65, -809.62) * mm});
            skLineSegment(sketch, "E280.top", {"start": v(-3841.75, -771.53) * mm, "end": v(-3803.65, -771.53) * mm});
            skLineSegment(sketch, "E280.left", {"start": v(-3841.75, -809.62) * mm, "end": v(-3841.75, -771.53) * mm});
            skLineSegment(sketch, "E280.right", {"start": v(-3803.65, -809.62) * mm, "end": v(-3803.65, -771.53) * mm});
            skLineSegment(sketch, "E281.0", {"start": v(-3282.95, -809.62) * mm, "end": v(-3282.95, -771.53) * mm, "construction": true});
            skLineSegment(sketch, "E282.bottom", {"start": v(-3282.95, -809.62) * mm, "end": v(-3321.05, -809.62) * mm});
            skLineSegment(sketch, "E282.top", {"start": v(-3282.95, -771.53) * mm, "end": v(-3321.05, -771.53) * mm});
            skLineSegment(sketch, "E282.left", {"start": v(-3282.95, -809.62) * mm, "end": v(-3282.95, -771.53) * mm});
            skLineSegment(sketch, "E282.right", {"start": v(-3321.05, -809.62) * mm, "end": v(-3321.05, -771.53) * mm});
            skPoint(sketch, "E283.0", {"position": v(-3244.85, -809.62) * mm});
            skLineSegment(sketch, "E284.bottom", {"start": v(-3206.75, -809.62) * mm, "end": v(-3244.85, -809.62) * mm});
            skLineSegment(sketch, "E284.top", {"start": v(-3206.75, -771.52) * mm, "end": v(-3244.85, -771.52) * mm});
            skLineSegment(sketch, "E284.left", {"start": v(-3206.75, -809.62) * mm, "end": v(-3206.75, -771.52) * mm});
            skLineSegment(sketch, "E284.right", {"start": v(-3244.85, -809.62) * mm, "end": v(-3244.85, -771.52) * mm});
            skLineSegment(sketch, "E285.bottom", {"start": v(-2876.55, -809.62) * mm, "end": v(-2914.65, -809.62) * mm});
            skLineSegment(sketch, "E285.top", {"start": v(-2876.55, -771.53) * mm, "end": v(-2914.65, -771.53) * mm});
            skLineSegment(sketch, "E285.left", {"start": v(-2876.55, -809.62) * mm, "end": v(-2876.55, -771.53) * mm});
            skLineSegment(sketch, "E285.right", {"start": v(-2914.65, -809.62) * mm, "end": v(-2914.65, -771.53) * mm});
            skLineSegment(sketch, "E286.bottom", {"start": v(-1860.55, -809.62) * mm, "end": v(-1898.65, -809.62) * mm});
            skLineSegment(sketch, "E286.top", {"start": v(-1860.55, -771.53) * mm, "end": v(-1898.65, -771.53) * mm});
            skLineSegment(sketch, "E286.left", {"start": v(-1860.55, -809.62) * mm, "end": v(-1860.55, -771.53) * mm});
            skLineSegment(sketch, "E286.right", {"start": v(-1898.65, -809.62) * mm, "end": v(-1898.65, -771.53) * mm});
            skLineSegment(sketch, "E287.bottom", {"start": v(-2190.75, -809.62) * mm, "end": v(-2228.85, -809.62) * mm});
            skLineSegment(sketch, "E287.top", {"start": v(-2190.75, -771.53) * mm, "end": v(-2228.85, -771.53) * mm});
            skLineSegment(sketch, "E287.left", {"start": v(-2190.75, -809.62) * mm, "end": v(-2190.75, -771.53) * mm});
            skLineSegment(sketch, "E287.right", {"start": v(-2228.85, -809.62) * mm, "end": v(-2228.85, -771.53) * mm});
            skLineSegment(sketch, "E288.bottom", {"start": v(-1149.35, -809.62) * mm, "end": v(-1187.45, -809.62) * mm});
            skLineSegment(sketch, "E288.top", {"start": v(-1149.35, -771.53) * mm, "end": v(-1187.45, -771.53) * mm});
            skLineSegment(sketch, "E288.left", {"start": v(-1149.35, -809.62) * mm, "end": v(-1149.35, -771.53) * mm});
            skLineSegment(sketch, "E288.right", {"start": v(-1187.45, -809.62) * mm, "end": v(-1187.45, -771.53) * mm});
            skLineSegment(sketch, "E289.bottom", {"start": v(-19.05, -809.62) * mm, "end": v(-57.15, -809.62) * mm});
            skLineSegment(sketch, "E289.top", {"start": v(-19.05, -771.53) * mm, "end": v(-57.15, -771.53) * mm});
            skLineSegment(sketch, "E289.left", {"start": v(-19.05, -809.62) * mm, "end": v(-19.05, -771.53) * mm});
            skLineSegment(sketch, "E289.right", {"start": v(-57.15, -809.62) * mm, "end": v(-57.15, -771.53) * mm});
            skSolve(sketch);
        }
        {
            var Q0;
            Q0 = qSketchRegion(id + "F55", true);
            var Q1;
            Q1=makeQuery(id+"F5.opExtrude","SWEPT_FACE",FACE,{"disambiguationData":[OSD([sQuery(id+"F4.wireOp",EDGE,"E19.right")])]});
            extrude(context, id + "F56", {"entities" : qUnion([Q0]), "endBound" : BoundingType.UP_TO_SURFACE, "depth" : 25.4 * mm, "endBoundEntityFace" : qUnion([Q1]), "offsetDistance" : 25.4 * mm});
        }
        {
            var Q0;
            Q0=makeQuery(id+"F13.opExtrude","SWEPT_FACE",FACE,{"disambiguationData":[OSD([sQuery(id+"F12.wireOp",EDGE,"E36.bottom")])]});
            var sketch = newSketch(context, id + "F57", { "sketchPlane" : qUnion([Q0])});
            skPoint(sketch, "E290.0", {"position": v(-1841.5, 0) * mm});
            skPoint(sketch, "E291.0", {"position": v(-1860.55, -19.05) * mm});
            skLineSegment(sketch, "E292.bottom", {"start": v(-3860.8, 19.05) * mm, "end": v(-1841.5, 19.05) * mm});
            skLineSegment(sketch, "E292.top", {"start": v(-3860.8, -31.75) * mm, "end": v(-1841.5, -31.75) * mm});
            skLineSegment(sketch, "E292.left", {"start": v(-3860.8, 19.05) * mm, "end": v(-3860.8, -31.75) * mm});
            skLineSegment(sketch, "E292.right", {"start": v(-1841.5, 19.05) * mm, "end": v(-1841.5, -31.75) * mm});
            skPoint(sketch, "E293.0", {"position": v(-19.05, -19.05) * mm});
            skPoint(sketch, "E293.1", {"position": v(0, 0) * mm});
            skPoint(sketch, "E294.0", {"position": v(-1206.5, 19.05) * mm});
            skLineSegment(sketch, "E295.bottom", {"start": v(-1206.5, 19.05) * mm, "end": v(0, 19.05) * mm});
            skLineSegment(sketch, "E295.top", {"start": v(-1206.5, -31.75) * mm, "end": v(0, -31.75) * mm});
            skLineSegment(sketch, "E295.left", {"start": v(-1206.5, 19.05) * mm, "end": v(-1206.5, -31.75) * mm});
            skLineSegment(sketch, "E295.right", {"start": v(0, 19.05) * mm, "end": v(0, -31.75) * mm});
            skPoint(sketch, "E296.0", {"position": v(-3263.9, -809.62) * mm});
            skLineSegment(sketch, "E297.bottom", {"start": v(-3860.8, -809.62) * mm, "end": v(-3263.9, -809.62) * mm});
            skLineSegment(sketch, "E297.top", {"start": v(-3860.8, -771.53) * mm, "end": v(-3263.9, -771.53) * mm});
            skLineSegment(sketch, "E297.left", {"start": v(-3860.8, -809.62) * mm, "end": v(-3860.8, -771.53) * mm});
            skLineSegment(sketch, "E297.right", {"start": v(-3263.9, -809.62) * mm, "end": v(-3263.9, -771.53) * mm});
            skLineSegment(sketch, "E298.bottom", {"start": v(-2247.9, -809.62) * mm, "end": v(-1841.5, -809.62) * mm});
            skLineSegment(sketch, "E298.top", {"start": v(-2247.9, -720.73) * mm, "end": v(-1841.5, -720.73) * mm});
            skLineSegment(sketch, "E298.left", {"start": v(-2247.9, -809.62) * mm, "end": v(-2247.9, -720.73) * mm});
            skLineSegment(sketch, "E298.right", {"start": v(-1841.5, -809.62) * mm, "end": v(-1841.5, -720.73) * mm});
            skLineSegment(sketch, "E299.bottom", {"start": v(-1206.5, -809.62) * mm, "end": v(0, -809.62) * mm});
            skLineSegment(sketch, "E299.top", {"start": v(-1206.5, -720.73) * mm, "end": v(0, -720.73) * mm});
            skLineSegment(sketch, "E299.left", {"start": v(-1206.5, -809.62) * mm, "end": v(-1206.5, -720.73) * mm});
            skLineSegment(sketch, "E299.right", {"start": v(0, -809.62) * mm, "end": v(0, -720.73) * mm});
            skSolve(sketch);
        }
        {
            var Q0;
            Q0 = qSketchRegion(id + "F57", true);
            extrude(context, id + "F58", {"entities" : qUnion([Q0]), "depth" : 19.05 * mm, "offsetDistance" : 25.4 * mm});
        }
        {
            var Q0;
            Q0=makeQuery(id+"F36.opExtrude","SWEPT_FACE",FACE,{"disambiguationData":[OSD([sQuery(id+"F35.wireOp",EDGE,"E76.bottom")])]});
            var sketch = newSketch(context, id + "F59", { "sketchPlane" : qUnion([Q0])});
            skLineSegment(sketch, "E300.bottom", {"start": v(-3860.8, 914.4) * mm, "end": v(-2562.22, 914.4) * mm});
            skLineSegment(sketch, "E300.top", {"start": v(-3860.8, 247.65) * mm, "end": v(-2562.22, 247.65) * mm});
            skLineSegment(sketch, "E300.left", {"start": v(-3860.8, 914.4) * mm, "end": v(-3860.8, 247.65) * mm});
            skLineSegment(sketch, "E300.right", {"start": v(-2562.22, 914.4) * mm, "end": v(-2562.22, 247.65) * mm});
            skSolve(sketch);
        }
        {
            var Q0;
            Q0 = qSketchRegion(id + "F59", true);
            extrude(context, id + "F60", {"entities" : qUnion([Q0]), "depth" : 19.05 * mm, "offsetDistance" : 25.4 * mm});
        }
        {
            var Q0;
            Q0=makeQuery(id+"F40.opExtrude","SWEPT_FACE",FACE,{"disambiguationData":[OSD([sQuery(id+"F39.wireOp",EDGE,"E83.0.1")])]});
            var sketch = newSketch(context, id + "F61", { "sketchPlane" : qUnion([Q0])});
            skLineSegment(sketch, "E301.bottom", {"start": v(-2562.22, 914.4) * mm, "end": v(-635, 914.4) * mm});
            skLineSegment(sketch, "E301.top", {"start": v(-2562.22, 247.65) * mm, "end": v(-635, 247.65) * mm});
            skLineSegment(sketch, "E301.left", {"start": v(-2562.22, 914.4) * mm, "end": v(-2562.22, 247.65) * mm});
            skLineSegment(sketch, "E301.right", {"start": v(-635, 914.4) * mm, "end": v(-635, 247.65) * mm});
            skSolve(sketch);
        }
        {
            var Q0;
            Q0 = qSketchRegion(id + "F61", true);
            var Q1;
            Q1=makeQuery(id+"F60.opExtrude","CAP_FACE",FACE,{"disambiguationData":[OSD([sQuery(id+"F59.wireOp",EDGE,"E300.bottom"),sQuery(id+"F59.wireOp",EDGE,"E300.top"),sQuery(id+"F59.wireOp",EDGE,"E300.left"),sQuery(id+"F59.wireOp",EDGE,"E300.right")])],"isStart":false});
            extrude(context, id + "F62", {"entities" : qUnion([Q0]), "endBound" : BoundingType.UP_TO_SURFACE, "depth" : 25.4 * mm, "endBoundEntityFace" : qUnion([Q1]), "offsetDistance" : 25.4 * mm});
        }
        {
            var Q0;
            Q0=makeQuery(id+"F60.opExtrude","CAP_FACE",FACE,{"disambiguationData":[OSD([sQuery(id+"F59.wireOp",EDGE,"E300.bottom"),sQuery(id+"F59.wireOp",EDGE,"E300.top"),sQuery(id+"F59.wireOp",EDGE,"E300.left"),sQuery(id+"F59.wireOp",EDGE,"E300.right")])],"isStart":false});
            var sketch = newSketch(context, id + "F63", { "sketchPlane" : qUnion([Q0])});
            skLineSegment(sketch, "E302.bottom", {"start": v(-3073.4, 650.88) * mm, "end": v(-635, 650.88) * mm});
            skLineSegment(sketch, "E302.top", {"start": v(-3073.4, 247.65) * mm, "end": v(-635, 247.65) * mm});
            skLineSegment(sketch, "E302.left", {"start": v(-3073.4, 650.88) * mm, "end": v(-3073.4, 247.65) * mm});
            skLineSegment(sketch, "E302.right", {"start": v(-635, 650.88) * mm, "end": v(-635, 247.65) * mm});
            skSolve(sketch);
        }
        {
            var Q0;
            Q0 = qSketchRegion(id + "F63", true);
            extrude(context, id + "F64", {"entities" : qUnion([Q0]), "depth" : 19.05 * mm, "offsetDistance" : 25.4 * mm});
        }
        {
            var Q0;
            Q0=makeQuery(id+"F64.opExtrude","CAP_FACE",FACE,{"disambiguationData":[OSD([sQuery(id+"F63.wireOp",EDGE,"E302.bottom"),sQuery(id+"F63.wireOp",EDGE,"E302.top"),sQuery(id+"F63.wireOp",EDGE,"E302.left"),sQuery(id+"F63.wireOp",EDGE,"E302.right")])],"isStart":false});
            var sketch = newSketch(context, id + "F65", { "sketchPlane" : qUnion([Q0])});
            skLineSegment(sketch, "E303.bottom", {"start": v(-3073.4, 650.87) * mm, "end": v(-3054.35, 650.87) * mm});
            skLineSegment(sketch, "E303.top", {"start": v(-3073.4, 247.65) * mm, "end": v(-3054.35, 247.65) * mm});
            skLineSegment(sketch, "E303.left", {"start": v(-3073.4, 650.88) * mm, "end": v(-3073.4, 247.65) * mm});
            skLineSegment(sketch, "E303.right", {"start": v(-3054.35, 650.87) * mm, "end": v(-3054.35, 247.65) * mm});
            skLineSegment(sketch, "E304.bottom", {"start": v(-654.05, 650.88) * mm, "end": v(-635, 650.88) * mm});
            skLineSegment(sketch, "E304.top", {"start": v(-654.05, 247.65) * mm, "end": v(-635, 247.65) * mm});
            skLineSegment(sketch, "E304.left", {"start": v(-654.05, 650.88) * mm, "end": v(-654.05, 247.65) * mm});
            skLineSegment(sketch, "E304.right", {"start": v(-635, 650.88) * mm, "end": v(-635, 247.65) * mm});
            skLineSegment(sketch, "E305.bottom", {"start": v(-1863.72, 650.88) * mm, "end": v(-1844.67, 650.88) * mm});
            skLineSegment(sketch, "E305.top", {"start": v(-1863.72, 247.65) * mm, "end": v(-1844.67, 247.65) * mm});
            skLineSegment(sketch, "E305.left", {"start": v(-1863.72, 650.88) * mm, "end": v(-1863.72, 247.65) * mm});
            skLineSegment(sketch, "E305.right", {"start": v(-1844.67, 650.88) * mm, "end": v(-1844.67, 247.65) * mm});
            skLineSegment(sketch, "E306", {"start": v(-1854.2, 650.88) * mm, "end": v(-1854.2, 247.65) * mm, "construction": true});
            skLineSegment(sketch, "E307.bottom", {"start": v(-2673.35, 650.88) * mm, "end": v(-2660.65, 650.88) * mm});
            skLineSegment(sketch, "E307.top", {"start": v(-2673.35, 247.65) * mm, "end": v(-2660.65, 247.65) * mm});
            skLineSegment(sketch, "E307.left", {"start": v(-2673.35, 650.88) * mm, "end": v(-2673.35, 247.65) * mm});
            skLineSegment(sketch, "E307.right", {"start": v(-2660.65, 650.87) * mm, "end": v(-2660.65, 247.65) * mm});
            skLineSegment(sketch, "E308.bottom", {"start": v(-2257.43, 650.88) * mm, "end": v(-2244.72, 650.88) * mm});
            skLineSegment(sketch, "E308.top", {"start": v(-2257.43, 247.65) * mm, "end": v(-2244.72, 247.65) * mm});
            skLineSegment(sketch, "E308.left", {"start": v(-2257.43, 650.87) * mm, "end": v(-2257.43, 247.65) * mm});
            skLineSegment(sketch, "E308.right", {"start": v(-2244.72, 650.88) * mm, "end": v(-2244.72, 247.65) * mm});
            skLineSegment(sketch, "E309.MirrorCS", {"start": v(-1035.05, 650.88) * mm, "end": v(-1047.75, 650.88) * mm});
            skLineSegment(sketch, "E310.MirrorCS", {"start": v(-1450.97, 650.88) * mm, "end": v(-1463.67, 650.88) * mm});
            skLineSegment(sketch, "E311.MirrorCS", {"start": v(-1035.05, 247.65) * mm, "end": v(-1047.75, 247.65) * mm});
            skLineSegment(sketch, "E312.MirrorCS", {"start": v(-1450.97, 247.65) * mm, "end": v(-1463.67, 247.65) * mm});
            skLineSegment(sketch, "E313.MirrorCS", {"start": v(-1450.97, 650.88) * mm, "end": v(-1450.97, 247.65) * mm});
            skLineSegment(sketch, "E314.MirrorCS", {"start": v(-1463.67, 650.88) * mm, "end": v(-1463.67, 247.65) * mm});
            skLineSegment(sketch, "E315.MirrorCS", {"start": v(-1047.75, 650.88) * mm, "end": v(-1047.75, 247.65) * mm});
            skLineSegment(sketch, "E316.MirrorCS", {"start": v(-1035.05, 650.88) * mm, "end": v(-1035.05, 247.65) * mm});
            skSolve(sketch);
        }
        {
            var Q0;
            Q0 = qSketchRegion(id + "F65", true);
            extrude(context, id + "F66", {"entities" : qUnion([Q0]), "depth" : 317.5 * mm, "offsetDistance" : 25.4 * mm});
        }
        {
            var Q0;
            Q0=makeQuery(id+"F66.opExtrude","CAP_FACE",FACE,{"disambiguationData":[OSD([sQuery(id+"F65.wireOp",EDGE,"E303.bottom"),sQuery(id+"F65.wireOp",EDGE,"E303.top"),sQuery(id+"F65.wireOp",EDGE,"E303.left"),sQuery(id+"F65.wireOp",EDGE,"E303.right")])],"isStart":false});
            var sketch = newSketch(context, id + "F67", { "sketchPlane" : qUnion([Q0])});
            skLineSegment(sketch, "E317.0.0", {"start": v(-635, 650.88) * mm, "end": v(-3073.4, 650.88) * mm});
            skLineSegment(sketch, "E317.0.1", {"start": v(-3073.4, 650.88) * mm, "end": v(-3073.4, 247.65) * mm});
            skLineSegment(sketch, "E317.0.2", {"start": v(-3073.4, 247.65) * mm, "end": v(-635, 247.65) * mm});
            skLineSegment(sketch, "E317.0.3", {"start": v(-635, 247.65) * mm, "end": v(-635, 650.88) * mm});
            skSolve(sketch);
        }
        {
            var Q0;
            Q0 = qSketchRegion(id + "F67", true);
            extrude(context, id + "F68", {"entities" : qUnion([Q0]), "depth" : 19.05 * mm, "offsetDistance" : 25.4 * mm});
        }
        {
            var Q0;
            Q0=makeQuery(id+"F60.opExtrude","CAP_FACE",FACE,{"disambiguationData":[OSD([sQuery(id+"F59.wireOp",EDGE,"E300.bottom"),sQuery(id+"F59.wireOp",EDGE,"E300.top"),sQuery(id+"F59.wireOp",EDGE,"E300.left"),sQuery(id+"F59.wireOp",EDGE,"E300.right")])],"isStart":false});
            var sketch = newSketch(context, id + "F69", { "sketchPlane" : qUnion([Q0])});
            skLineSegment(sketch, "E318.bottom", {"start": v(-3860.8, 650.88) * mm, "end": v(-3073.4, 650.88) * mm});
            skLineSegment(sketch, "E318.top", {"start": v(-3860.8, 247.65) * mm, "end": v(-3073.4, 247.65) * mm});
            skLineSegment(sketch, "E318.left", {"start": v(-3860.8, 650.88) * mm, "end": v(-3860.8, 247.65) * mm});
            skLineSegment(sketch, "E318.right", {"start": v(-3073.4, 650.88) * mm, "end": v(-3073.4, 247.65) * mm});
            skSolve(sketch);
        }
        {
            var Q0;
            Q0 = qSketchRegion(id + "F69", true);
            var Q1;
            Q1=makeQuery(id+"F64.opExtrude","CAP_FACE",FACE,{"disambiguationData":[OSD([sQuery(id+"F63.wireOp",EDGE,"E302.bottom"),sQuery(id+"F63.wireOp",EDGE,"E302.top"),sQuery(id+"F63.wireOp",EDGE,"E302.left"),sQuery(id+"F63.wireOp",EDGE,"E302.right")])],"isStart":false});
            extrude(context, id + "F70", {"entities" : qUnion([Q0]), "endBound" : BoundingType.UP_TO_SURFACE, "depth" : 25.4 * mm, "endBoundEntityFace" : qUnion([Q1]), "offsetDistance" : 25.4 * mm});
        }
        {
            var Q0;
            Q0=makeQuery(id+"F70.opExtrude","CAP_FACE",FACE,{"disambiguationData":[OSD([sQuery(id+"F69.wireOp",EDGE,"E318.bottom"),sQuery(id+"F69.wireOp",EDGE,"E318.top"),sQuery(id+"F69.wireOp",EDGE,"E318.left"),sQuery(id+"F69.wireOp",EDGE,"E318.right")])],"isStart":false});
            var sketch = newSketch(context, id + "F71", { "sketchPlane" : qUnion([Q0])});
            skLineSegment(sketch, "E319.bottom", {"start": v(-3860.8, 650.88) * mm, "end": v(-3841.75, 650.88) * mm});
            skLineSegment(sketch, "E319.top", {"start": v(-3860.8, 247.65) * mm, "end": v(-3841.75, 247.65) * mm});
            skLineSegment(sketch, "E319.left", {"start": v(-3860.8, 650.88) * mm, "end": v(-3860.8, 247.65) * mm});
            skLineSegment(sketch, "E319.right", {"start": v(-3841.75, 650.88) * mm, "end": v(-3841.75, 247.65) * mm});
            skLineSegment(sketch, "E320.bottom", {"start": v(-3073.4, 650.88) * mm, "end": v(-3092.45, 650.88) * mm});
            skLineSegment(sketch, "E320.top", {"start": v(-3073.4, 247.65) * mm, "end": v(-3092.45, 247.65) * mm});
            skLineSegment(sketch, "E320.left", {"start": v(-3073.4, 650.88) * mm, "end": v(-3073.4, 247.65) * mm});
            skLineSegment(sketch, "E320.right", {"start": v(-3092.45, 650.88) * mm, "end": v(-3092.45, 247.65) * mm});
            skSolve(sketch);
        }
        {
            var Q0;
            Q0 = qSketchRegion(id + "F71", true);
            var Q1;
            Q1=makeQuery(id+"F68.opExtrude","CAP_FACE",FACE,{"disambiguationData":[OSD([sQuery(id+"F67.wireOp",EDGE,"E317.0.0"),sQuery(id+"F67.wireOp",EDGE,"E317.0.1"),sQuery(id+"F67.wireOp",EDGE,"E317.0.2"),sQuery(id+"F67.wireOp",EDGE,"E317.0.3")])],"isStart":true});
            extrude(context, id + "F72", {"entities" : qUnion([Q0]), "endBound" : BoundingType.UP_TO_SURFACE, "depth" : 25.4 * mm, "endBoundEntityFace" : qUnion([Q1]), "offsetDistance" : 25.4 * mm});
        }
        {
            var Q0;
            Q0=makeQuery(id+"F72.opExtrude","CAP_FACE",FACE,{"disambiguationData":[OSD([sQuery(id+"F71.wireOp",EDGE,"E319.bottom"),sQuery(id+"F71.wireOp",EDGE,"E319.top"),sQuery(id+"F71.wireOp",EDGE,"E319.left"),sQuery(id+"F71.wireOp",EDGE,"E319.right")])],"isStart":false});
            var sketch = newSketch(context, id + "F73", { "sketchPlane" : qUnion([Q0])});
            skLineSegment(sketch, "E321.0.0", {"start": v(-3073.4, 247.65) * mm, "end": v(-3073.4, 650.88) * mm});
            skLineSegment(sketch, "E321.0.1", {"start": v(-3073.4, 650.88) * mm, "end": v(-3860.8, 650.88) * mm});
            skLineSegment(sketch, "E321.0.2", {"start": v(-3860.8, 650.88) * mm, "end": v(-3860.8, 247.65) * mm});
            skLineSegment(sketch, "E321.0.3", {"start": v(-3860.8, 247.65) * mm, "end": v(-3073.4, 247.65) * mm});
            skSolve(sketch);
        }
        {
            var Q0;
            Q0 = qSketchRegion(id + "F73", true);
            var Q1;
            Q1=makeQuery(id+"F68.opExtrude","CAP_FACE",FACE,{"disambiguationData":[OSD([sQuery(id+"F67.wireOp",EDGE,"E317.0.0"),sQuery(id+"F67.wireOp",EDGE,"E317.0.1"),sQuery(id+"F67.wireOp",EDGE,"E317.0.2"),sQuery(id+"F67.wireOp",EDGE,"E317.0.3")])],"isStart":false});
            extrude(context, id + "F74", {"entities" : qUnion([Q0]), "endBound" : BoundingType.UP_TO_SURFACE, "depth" : 25.4 * mm, "endBoundEntityFace" : qUnion([Q1]), "offsetDistance" : 25.4 * mm});
        }
        {
            var Q0;
            Q0=makeQuery(id+"F66.opExtrude","SWEPT_FACE",FACE,{"disambiguationData":[OSD([sQuery(id+"F65.wireOp",EDGE,"E304.bottom")])]});
            var sketch = newSketch(context, id + "F75", { "sketchPlane" : qUnion([Q0])});
            skLineSegment(sketch, "E322.bottom", {"start": v(635, 977.9) * mm, "end": v(3073.4, 977.9) * mm});
            skLineSegment(sketch, "E322.top", {"start": v(635, 622.3) * mm, "end": v(3073.4, 622.3) * mm});
            skLineSegment(sketch, "E322.left", {"start": v(635, 977.9) * mm, "end": v(635, 622.3) * mm});
            skLineSegment(sketch, "E322.right", {"start": v(3073.4, 977.9) * mm, "end": v(3073.4, 622.3) * mm});
            skSolve(sketch);
        }
        {
            var Q0;
            Q0 = qSketchRegion(id + "F75", true);
            extrude(context, id + "F76", {"entities" : qUnion([Q0]), "depth" : 6.35 * mm, "offsetDistance" : 25.4 * mm});
        }
        {
            var Q0;
            Q0=makeQuery(id+"F74.opExtrude","SWEPT_FACE",FACE,{"disambiguationData":[OSD([sQuery(id+"F73.wireOp",EDGE,"E321.0.1")])]});
            var sketch = newSketch(context, id + "F77", { "sketchPlane" : qUnion([Q0])});
            skLineSegment(sketch, "E323.bottom", {"start": v(3073.4, 977.9) * mm, "end": v(3860.8, 977.9) * mm});
            skLineSegment(sketch, "E323.top", {"start": v(3073.4, 622.3) * mm, "end": v(3860.8, 622.3) * mm});
            skLineSegment(sketch, "E323.left", {"start": v(3073.4, 977.9) * mm, "end": v(3073.4, 622.3) * mm});
            skLineSegment(sketch, "E323.right", {"start": v(3860.8, 977.9) * mm, "end": v(3860.8, 622.3) * mm});
            skSolve(sketch);
        }
        {
            var Q0;
            Q0 = qSketchRegion(id + "F77", true);
            var Q1;
            Q1=makeQuery(id+"F76.opExtrude","CAP_FACE",FACE,{"disambiguationData":[OSD([sQuery(id+"F75.wireOp",EDGE,"E322.bottom"),sQuery(id+"F75.wireOp",EDGE,"E322.top"),sQuery(id+"F75.wireOp",EDGE,"E322.left"),sQuery(id+"F75.wireOp",EDGE,"E322.right")])],"isStart":false});
            extrude(context, id + "F78", {"entities" : qUnion([Q0]), "endBound" : BoundingType.UP_TO_SURFACE, "depth" : 25.4 * mm, "endBoundEntityFace" : qUnion([Q1]), "offsetDistance" : 25.4 * mm});
        }
        {
            var Q0;
            Q0=makeQuery(id+"F70.opExtrude","SWEPT_FACE",FACE,{"disambiguationData":[OSD([sQuery(id+"F69.wireOp",EDGE,"E318.top")])]});
            var sketch = newSketch(context, id + "F79", { "sketchPlane" : qUnion([Q0])});
            skLineSegment(sketch, "E324.bottom", {"start": v(-3860.8, 641.35) * mm, "end": v(-3073.4, 641.35) * mm});
            skLineSegment(sketch, "E324.top", {"start": v(-3860.8, 603.25) * mm, "end": v(-3073.4, 603.25) * mm});
            skLineSegment(sketch, "E324.left", {"start": v(-3860.8, 641.35) * mm, "end": v(-3860.8, 603.25) * mm});
            skLineSegment(sketch, "E324.right", {"start": v(-3073.4, 641.35) * mm, "end": v(-3073.4, 603.25) * mm});
            skSolve(sketch);
        }
        {
            var Q0;
            Q0=makeQuery(id+"F66.opExtrude","SWEPT_FACE",FACE,{"disambiguationData":[OSD([sQuery(id+"F65.wireOp",EDGE,"E303.top")])]});
            var sketch = newSketch(context, id + "F80", { "sketchPlane" : qUnion([Q0])});
            skLineSegment(sketch, "E325.bottom", {"start": v(-3073.4, 641.35) * mm, "end": v(-635, 641.35) * mm});
            skLineSegment(sketch, "E325.top", {"start": v(-3073.4, 603.25) * mm, "end": v(-635, 603.25) * mm});
            skLineSegment(sketch, "E325.left", {"start": v(-3073.4, 641.35) * mm, "end": v(-3073.4, 603.25) * mm});
            skLineSegment(sketch, "E325.right", {"start": v(-635, 641.35) * mm, "end": v(-635, 603.25) * mm});
            skSolve(sketch);
        }
        {
            var Q0;
            Q0 = qSketchRegion(id + "F79", true);
            extrude(context, id + "F81", {"entities" : qUnion([Q0]), "depth" : 19.05 * mm, "offsetDistance" : 25.4 * mm});
        }
        {
            var Q0;
            Q0 = qSketchRegion(id + "F80", true);
            var Q1;
            Q1=makeQuery(id+"F81.opExtrude","CAP_FACE",FACE,{"disambiguationData":[OSD([sQuery(id+"F79.wireOp",EDGE,"E324.bottom"),sQuery(id+"F79.wireOp",EDGE,"E324.top"),sQuery(id+"F79.wireOp",EDGE,"E324.left"),sQuery(id+"F79.wireOp",EDGE,"E324.right")])],"isStart":false});
            extrude(context, id + "F82", {"entities" : qUnion([Q0]), "endBound" : BoundingType.UP_TO_SURFACE, "depth" : 25.4 * mm, "endBoundEntityFace" : qUnion([Q1]), "offsetDistance" : 25.4 * mm});
        }
    });
